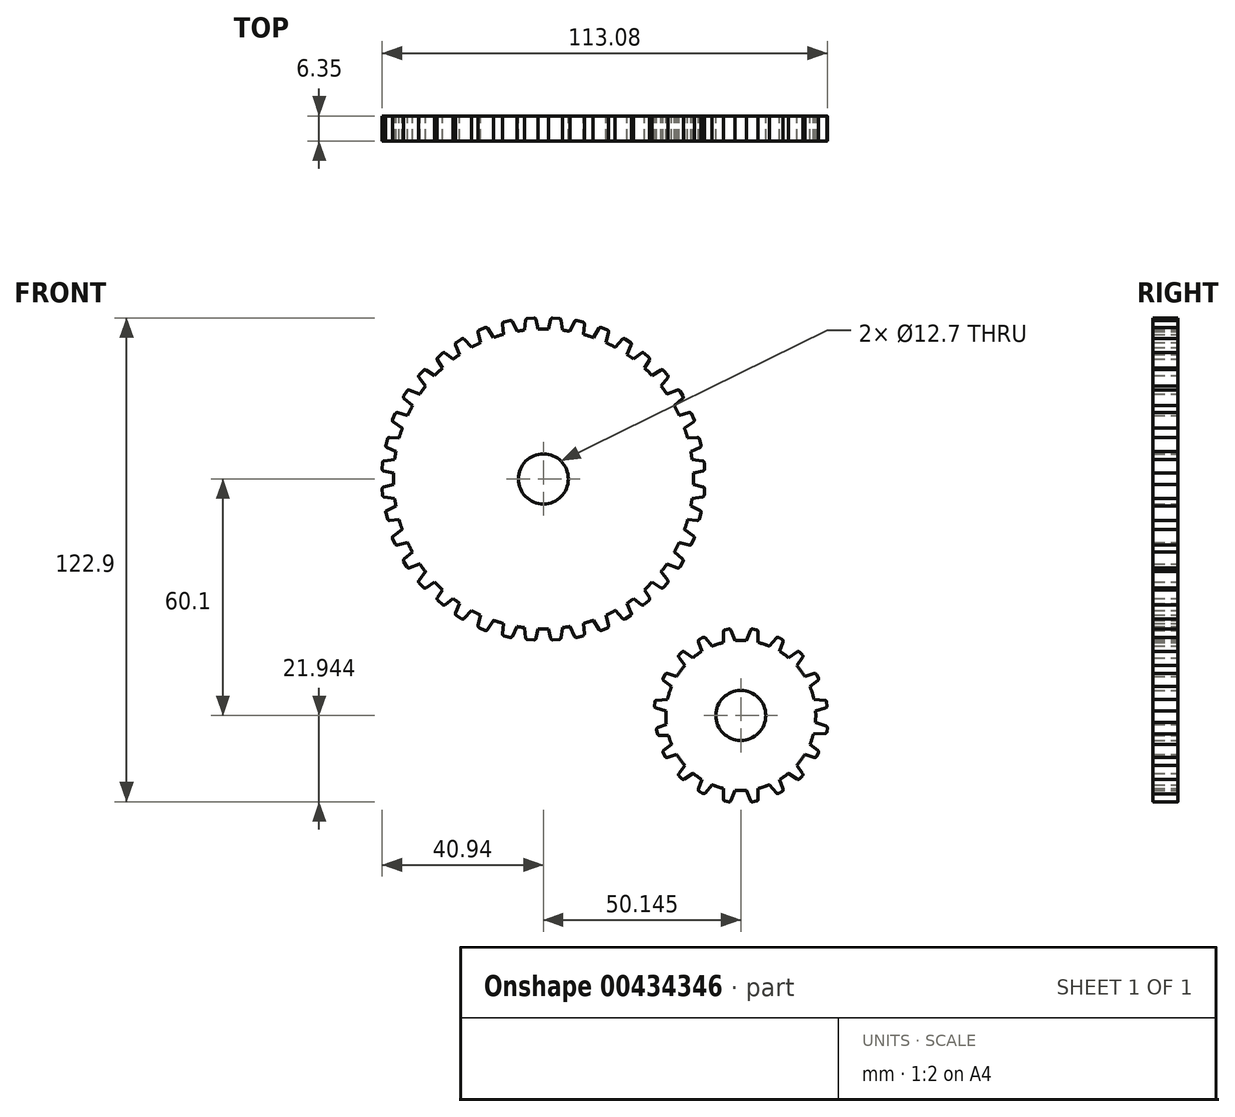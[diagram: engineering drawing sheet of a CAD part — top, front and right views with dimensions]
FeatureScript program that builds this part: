
annotation { "Feature Type Name" : "Feature", "Feature Type Description" : "" }
export const myFeature = defineFeature(function(context is Context, id is Id, definition is map)
    precondition{}
    {
        {
            var Q0;
            Q0=qCreatedBy(makeId("Front.planeOp"),FACE);
            var sketch = newSketch(context, id + "F0", { "sketchPlane" : qUnion([Q0])});
            skCircle(sketch, "E0", {"center": v(-27.1, 27.65) * mm, "radius": 38.1 * mm});
            skCircle(sketch, "E1", {"center": v(-27.1, 27.65) * mm, "radius": 6.35 * mm});
            skLineSegment(sketch, "E2", {"start": v(10.04, 32.06) * mm, "end": v(10.15, 29.52) * mm});
            skLineSegment(sketch, "E3", {"start": v(13.33, 32.24) * mm, "end": v(10.6, 32.59) * mm});
            skLineSegment(sketch, "E4", {"start": v(10.77, 29.05) * mm, "end": v(13.45, 29.65) * mm});
            skLineSegment(sketch, "E5", {"start": v(13.77, 31.76) * mm, "end": v(13.84, 30.17) * mm});
            skPoint(sketch, "E6.visualSharp", {"position": v(13.75, 32.18) * mm});
            skArc(sketch, "E6.filletArc", {"start": v(13.77, 31.76) * mm, "mid": v(13.64, 32.08) * mm, "end": v(13.33, 32.24) * mm});
            skPoint(sketch, "E7.visualSharp", {"position": v(10, 32.67) * mm});
            skArc(sketch, "E7.filletArc", {"start": v(10.6, 32.59) * mm, "mid": v(10.2, 32.46) * mm, "end": v(10.04, 32.06) * mm});
            skArc(sketch, "E8.filletArc", {"start": v(10.15, 29.52) * mm, "mid": v(10.35, 29.14) * mm, "end": v(10.77, 29.05) * mm});
            skPoint(sketch, "E9.visualSharp", {"position": v(13.86, 29.75) * mm});
            skArc(sketch, "E9.filletArc", {"start": v(13.45, 29.65) * mm, "mid": v(13.74, 29.84) * mm, "end": v(13.84, 30.17) * mm});
            skLineSegment(sketch, "E10.0", {"start": v(13.86, 29.75) * mm, "end": v(13.75, 32.18) * mm, "construction": true});
            skLineSegment(sketch, "E11", {"start": v(6.96, 43.07) * mm, "end": v(8.03, 40.77) * mm});
            skLineSegment(sketch, "E12", {"start": v(9.93, 44.48) * mm, "end": v(7.28, 43.77) * mm});
            skLineSegment(sketch, "E13", {"start": v(8.78, 40.57) * mm, "end": v(11.03, 42.14) * mm});
            skLineSegment(sketch, "E14", {"start": v(10.52, 44.2) * mm, "end": v(11.2, 42.77) * mm});
            skPoint(sketch, "E15.visualSharp", {"position": v(10.34, 44.6) * mm});
            skArc(sketch, "E15.filletArc", {"start": v(10.52, 44.2) * mm, "mid": v(10.28, 44.45) * mm, "end": v(9.93, 44.48) * mm});
            skPoint(sketch, "E16.visualSharp", {"position": v(6.7, 43.62) * mm});
            skArc(sketch, "E16.filletArc", {"start": v(7.28, 43.77) * mm, "mid": v(6.96, 43.5) * mm, "end": v(6.96, 43.07) * mm});
            skPoint(sketch, "E17.visualSharp", {"position": v(8.29, 40.22) * mm});
            skArc(sketch, "E17.filletArc", {"start": v(8.03, 40.77) * mm, "mid": v(8.36, 40.5) * mm, "end": v(8.78, 40.57) * mm});
            skPoint(sketch, "E18.visualSharp", {"position": v(11.38, 42.38) * mm});
            skArc(sketch, "E18.filletArc", {"start": v(11.03, 42.14) * mm, "mid": v(11.23, 42.42) * mm, "end": v(11.2, 42.77) * mm});
            skLineSegment(sketch, "E19.0", {"start": v(11.38, 42.38) * mm, "end": v(10.34, 44.6) * mm, "construction": true});
            skLineSegment(sketch, "E20", {"start": v(4.05, 48.5) * mm, "end": v(5.33, 46.32) * mm});
            skLineSegment(sketch, "E21", {"start": v(6.97, 50.23) * mm, "end": v(4.3, 49.24) * mm});
            skLineSegment(sketch, "E22", {"start": v(6.1, 46.19) * mm, "end": v(8.26, 48.02) * mm});
            skLineSegment(sketch, "E23", {"start": v(7.58, 50) * mm, "end": v(8.37, 48.67) * mm});
            skPoint(sketch, "E24.visualSharp", {"position": v(7.37, 50.38) * mm});
            skArc(sketch, "E24.filletArc", {"start": v(7.58, 50) * mm, "mid": v(7.32, 50.23) * mm, "end": v(6.97, 50.23) * mm});
            skPoint(sketch, "E25.visualSharp", {"position": v(3.74, 49.03) * mm});
            skArc(sketch, "E25.filletArc", {"start": v(4.3, 49.24) * mm, "mid": v(4, 48.94) * mm, "end": v(4.05, 48.5) * mm});
            skPoint(sketch, "E26.visualSharp", {"position": v(5.63, 45.8) * mm});
            skArc(sketch, "E26.filletArc", {"start": v(5.33, 46.32) * mm, "mid": v(5.68, 46.07) * mm, "end": v(6.1, 46.19) * mm});
            skPoint(sketch, "E27.visualSharp", {"position": v(8.58, 48.3) * mm});
            skArc(sketch, "E27.filletArc", {"start": v(8.26, 48.02) * mm, "mid": v(8.43, 48.32) * mm, "end": v(8.37, 48.67) * mm});
            skLineSegment(sketch, "E28.0", {"start": v(8.58, 48.3) * mm, "end": v(7.37, 50.38) * mm, "construction": true});
            skLineSegment(sketch, "E29", {"start": v(0.34, 53.06) * mm, "end": v(2.06, 51.19) * mm});
            skLineSegment(sketch, "E30", {"start": v(2.75, 55.3) * mm, "end": v(0.44, 53.83) * mm});
            skLineSegment(sketch, "E31", {"start": v(2.84, 51.22) * mm, "end": v(4.5, 53.4) * mm});
            skLineSegment(sketch, "E32", {"start": v(3.4, 55.22) * mm, "end": v(4.47, 54.06) * mm});
            skPoint(sketch, "E33.visualSharp", {"position": v(3.1, 55.54) * mm});
            skArc(sketch, "E33.filletArc", {"start": v(3.4, 55.22) * mm, "mid": v(3.09, 55.38) * mm, "end": v(2.75, 55.3) * mm});
            skPoint(sketch, "E34.visualSharp", {"position": v(-0.07, 53.5) * mm});
            skArc(sketch, "E34.filletArc", {"start": v(0.44, 53.83) * mm, "mid": v(0.2, 53.47) * mm, "end": v(0.34, 53.06) * mm});
            skPoint(sketch, "E35.visualSharp", {"position": v(2.47, 50.74) * mm});
            skArc(sketch, "E35.filletArc", {"start": v(2.06, 51.19) * mm, "mid": v(2.46, 51.03) * mm, "end": v(2.84, 51.22) * mm});
            skPoint(sketch, "E36.visualSharp", {"position": v(4.76, 53.74) * mm});
            skArc(sketch, "E36.filletArc", {"start": v(4.5, 53.4) * mm, "mid": v(4.6, 53.74) * mm, "end": v(4.47, 54.06) * mm});
            skLineSegment(sketch, "E37.0", {"start": v(4.76, 53.74) * mm, "end": v(3.1, 55.54) * mm, "construction": true});
            skLineSegment(sketch, "E38", {"start": v(-8.73, 60.35) * mm, "end": v(-6.6, 58.97) * mm});
            skLineSegment(sketch, "E39", {"start": v(-6.96, 63.13) * mm, "end": v(-8.82, 61.12) * mm});
            skLineSegment(sketch, "E40", {"start": v(-5.85, 59.2) * mm, "end": v(-4.79, 61.73) * mm});
            skLineSegment(sketch, "E41", {"start": v(-6.31, 63.21) * mm, "end": v(-4.98, 62.35) * mm});
            skPoint(sketch, "E42.visualSharp", {"position": v(-6.67, 63.44) * mm});
            skArc(sketch, "E42.filletArc", {"start": v(-6.31, 63.21) * mm, "mid": v(-6.65, 63.29) * mm, "end": v(-6.96, 63.13) * mm});
            skPoint(sketch, "E43.visualSharp", {"position": v(-9.24, 60.68) * mm});
            skArc(sketch, "E43.filletArc", {"start": v(-8.82, 61.12) * mm, "mid": v(-8.96, 60.71) * mm, "end": v(-8.73, 60.35) * mm});
            skPoint(sketch, "E44.visualSharp", {"position": v(-6.09, 58.64) * mm});
            skArc(sketch, "E44.filletArc", {"start": v(-6.6, 58.97) * mm, "mid": v(-6.17, 58.91) * mm, "end": v(-5.85, 59.2) * mm});
            skPoint(sketch, "E45.visualSharp", {"position": v(-4.62, 62.12) * mm});
            skArc(sketch, "E45.filletArc", {"start": v(-4.79, 61.73) * mm, "mid": v(-4.77, 62.07) * mm, "end": v(-4.98, 62.35) * mm});
            skLineSegment(sketch, "E46.0", {"start": v(-4.62, 62.12) * mm, "end": v(-6.67, 63.44) * mm, "construction": true});
            skLineSegment(sketch, "E47", {"start": v(-14.2, 62.88) * mm, "end": v(-11.86, 61.89) * mm});
            skLineSegment(sketch, "E48", {"start": v(-12.92, 65.94) * mm, "end": v(-14.42, 63.62) * mm});
            skLineSegment(sketch, "E49", {"start": v(-11.16, 62.24) * mm, "end": v(-10.54, 64.93) * mm});
            skLineSegment(sketch, "E50", {"start": v(-12.3, 66.13) * mm, "end": v(-10.84, 65.51) * mm});
            skPoint(sketch, "E51.visualSharp", {"position": v(-12.69, 66.3) * mm});
            skArc(sketch, "E51.filletArc", {"start": v(-12.3, 66.13) * mm, "mid": v(-12.64, 66.15) * mm, "end": v(-12.92, 65.94) * mm});
            skPoint(sketch, "E52.visualSharp", {"position": v(-14.75, 63.12) * mm});
            skArc(sketch, "E52.filletArc", {"start": v(-14.42, 63.62) * mm, "mid": v(-14.48, 63.2) * mm, "end": v(-14.2, 62.88) * mm});
            skPoint(sketch, "E53.visualSharp", {"position": v(-11.3, 61.65) * mm});
            skArc(sketch, "E53.filletArc", {"start": v(-11.86, 61.89) * mm, "mid": v(-11.43, 61.9) * mm, "end": v(-11.16, 62.24) * mm});
            skPoint(sketch, "E54.visualSharp", {"position": v(-10.45, 65.34) * mm});
            skArc(sketch, "E54.filletArc", {"start": v(-10.54, 64.93) * mm, "mid": v(-10.59, 65.27) * mm, "end": v(-10.84, 65.51) * mm});
            skLineSegment(sketch, "E55.0", {"start": v(-10.45, 65.34) * mm, "end": v(-12.69, 66.3) * mm, "construction": true});
            skLineSegment(sketch, "E56", {"start": v(-20.02, 64.46) * mm, "end": v(-17.57, 63.8) * mm});
            skLineSegment(sketch, "E57", {"start": v(-19.2, 67.65) * mm, "end": v(-20.35, 65.17) * mm});
            skLineSegment(sketch, "E58", {"start": v(-16.93, 64.25) * mm, "end": v(-16.7, 66.98) * mm});
            skLineSegment(sketch, "E59", {"start": v(-18.6, 67.93) * mm, "end": v(-17.07, 67.52) * mm});
            skPoint(sketch, "E60.visualSharp", {"position": v(-19.02, 68.04) * mm});
            skArc(sketch, "E60.filletArc", {"start": v(-18.6, 67.93) * mm, "mid": v(-18.95, 67.9) * mm, "end": v(-19.2, 67.65) * mm});
            skPoint(sketch, "E61.visualSharp", {"position": v(-20.6, 64.62) * mm});
            skArc(sketch, "E61.filletArc", {"start": v(-20.35, 65.17) * mm, "mid": v(-20.35, 64.74) * mm, "end": v(-20.02, 64.46) * mm});
            skPoint(sketch, "E62.visualSharp", {"position": v(-16.98, 63.65) * mm});
            skArc(sketch, "E62.filletArc", {"start": v(-17.57, 63.8) * mm, "mid": v(-17.15, 63.88) * mm, "end": v(-16.93, 64.25) * mm});
            skPoint(sketch, "E63.visualSharp", {"position": v(-16.66, 67.4) * mm});
            skArc(sketch, "E63.filletArc", {"start": v(-16.7, 66.98) * mm, "mid": v(-16.79, 67.32) * mm, "end": v(-17.07, 67.52) * mm});
            skLineSegment(sketch, "E64.0", {"start": v(-16.66, 67.4) * mm, "end": v(-19.02, 68.04) * mm, "construction": true});
            skLineSegment(sketch, "E65", {"start": v(8.98, 37.34) * mm, "end": v(9.63, 34.89) * mm});
            skLineSegment(sketch, "E66", {"start": v(11.97, 38.2) * mm, "end": v(9.42, 37.98) * mm});
            skLineSegment(sketch, "E67", {"start": v(10.34, 34.56) * mm, "end": v(12.66, 35.63) * mm});
            skLineSegment(sketch, "E68", {"start": v(12.5, 37.82) * mm, "end": v(12.93, 36.22) * mm});
            skPoint(sketch, "E69.visualSharp", {"position": v(12.4, 38.23) * mm});
            skArc(sketch, "E69.filletArc", {"start": v(12.5, 37.82) * mm, "mid": v(12.3, 38.1) * mm, "end": v(11.97, 38.2) * mm});
            skPoint(sketch, "E70.visualSharp", {"position": v(8.82, 37.92) * mm});
            skArc(sketch, "E70.filletArc", {"start": v(9.42, 37.98) * mm, "mid": v(9.05, 37.76) * mm, "end": v(8.98, 37.34) * mm});
            skPoint(sketch, "E71.visualSharp", {"position": v(9.79, 34.3) * mm});
            skArc(sketch, "E71.filletArc", {"start": v(9.63, 34.89) * mm, "mid": v(9.9, 34.56) * mm, "end": v(10.34, 34.56) * mm});
            skPoint(sketch, "E72.visualSharp", {"position": v(13.04, 35.81) * mm});
            skArc(sketch, "E72.filletArc", {"start": v(12.66, 35.63) * mm, "mid": v(12.9, 35.88) * mm, "end": v(12.93, 36.22) * mm});
            skLineSegment(sketch, "E73.0", {"start": v(13.04, 35.81) * mm, "end": v(12.4, 38.23) * mm, "construction": true});
            skLineSegment(sketch, "E74", {"start": v(-25.32, 65) * mm, "end": v(-22.78, 64.91) * mm});
            skLineSegment(sketch, "E75", {"start": v(-25.27, 68.11) * mm, "end": v(-25.8, 65.6) * mm});
            skLineSegment(sketch, "E76", {"start": v(-22.26, 65.49) * mm, "end": v(-22.62, 68.02) * mm});
            skLineSegment(sketch, "E77", {"start": v(-24.76, 68.51) * mm, "end": v(-23.1, 68.46) * mm});
            skPoint(sketch, "E78.visualSharp", {"position": v(-25.18, 68.53) * mm});
            skArc(sketch, "E78.filletArc", {"start": v(-24.76, 68.51) * mm, "mid": v(-25.09, 68.4) * mm, "end": v(-25.27, 68.11) * mm});
            skPoint(sketch, "E79.visualSharp", {"position": v(-25.93, 65.02) * mm});
            skArc(sketch, "E79.filletArc", {"start": v(-25.8, 65.6) * mm, "mid": v(-25.7, 65.2) * mm, "end": v(-25.32, 65) * mm});
            skPoint(sketch, "E80.visualSharp", {"position": v(-22.18, 64.9) * mm});
            skArc(sketch, "E80.filletArc", {"start": v(-22.78, 64.91) * mm, "mid": v(-22.39, 65.08) * mm, "end": v(-22.26, 65.49) * mm});
            skPoint(sketch, "E81.visualSharp", {"position": v(-22.68, 68.44) * mm});
            skArc(sketch, "E81.filletArc", {"start": v(-22.62, 68.02) * mm, "mid": v(-22.79, 68.33) * mm, "end": v(-23.1, 68.46) * mm});
            skLineSegment(sketch, "E82.0", {"start": v(-22.68, 68.44) * mm, "end": v(-25.18, 68.53) * mm, "construction": true});
            skPoint(sketch, "E83.endSnap0", {"position": v(10.7, 38.09) * mm});
            skLineSegment(sketch, "E84", {"start": v(-27.1, 65.75) * mm, "end": v(-27.1, -10.45) * mm, "construction": true});
            skLineSegment(sketch, "E85", {"start": v(-65.2, 27.65) * mm, "end": v(11, 27.65) * mm, "construction": true});
            skLineSegment(sketch, "E86", {"start": v(-4.21, 57.29) * mm, "end": v(-2.34, 55.57) * mm});
            skLineSegment(sketch, "E87", {"start": v(-2.15, 59.62) * mm, "end": v(-4.18, 58.06) * mm});
            skLineSegment(sketch, "E88", {"start": v(-1.57, 55.68) * mm, "end": v(-0.2, 57.84) * mm});
            skLineSegment(sketch, "E89", {"start": v(-1.5, 59.6) * mm, "end": v(-0.28, 58.48) * mm});
            skPoint(sketch, "E90.visualSharp", {"position": v(-1.82, 59.88) * mm});
            skArc(sketch, "E90.filletArc", {"start": v(-1.5, 59.6) * mm, "mid": v(-1.82, 59.73) * mm, "end": v(-2.15, 59.62) * mm});
            skPoint(sketch, "E91.visualSharp", {"position": v(-4.66, 57.7) * mm});
            skArc(sketch, "E91.filletArc", {"start": v(-4.18, 58.06) * mm, "mid": v(-4.38, 57.68) * mm, "end": v(-4.21, 57.29) * mm});
            skPoint(sketch, "E92.visualSharp", {"position": v(-1.9, 55.16) * mm});
            skArc(sketch, "E92.filletArc", {"start": v(-2.34, 55.57) * mm, "mid": v(-1.93, 55.44) * mm, "end": v(-1.57, 55.68) * mm});
            skPoint(sketch, "E93.visualSharp", {"position": v(0.03, 58.2) * mm});
            skArc(sketch, "E93.filletArc", {"start": v(-0.2, 57.84) * mm, "mid": v(-0.12, 58.17) * mm, "end": v(-0.28, 58.48) * mm});
            skLineSegment(sketch, "E94.0", {"start": v(0.03, 58.2) * mm, "end": v(-1.82, 59.88) * mm, "construction": true});
            skLineSegment(sketch, "E95.MirrorCS", {"start": v(-57.6, 55.22) * mm, "end": v(-58.67, 54.06) * mm});
            skArc(sketch, "E96.MirrorCS", {"start": v(-29.44, 68.51) * mm, "mid": v(-29.11, 68.4) * mm, "end": v(-28.93, 68.11) * mm});
            skArc(sketch, "E97.MirrorCS", {"start": v(-37.5, 66.98) * mm, "mid": v(-37.41, 67.32) * mm, "end": v(-37.13, 67.52) * mm});
            skLineSegment(sketch, "E98.MirrorCS", {"start": v(-61.78, 50) * mm, "end": v(-62.57, 48.67) * mm});
            skArc(sketch, "E99.MirrorCS", {"start": v(-66.7, 37.82) * mm, "mid": v(-66.5, 38.1) * mm, "end": v(-66.17, 38.2) * mm});
            skArc(sketch, "E100.MirrorCS", {"start": v(-43.66, 64.93) * mm, "mid": v(-43.61, 65.27) * mm, "end": v(-43.36, 65.51) * mm});
            skArc(sketch, "E101.MirrorCS", {"start": v(-63.62, 37.98) * mm, "mid": v(-63.25, 37.76) * mm, "end": v(-63.18, 37.34) * mm});
            skArc(sketch, "E102.MirrorCS", {"start": v(-33.85, 65.17) * mm, "mid": v(-33.85, 64.74) * mm, "end": v(-34.18, 64.46) * mm});
            skArc(sketch, "E103.MirrorCS", {"start": v(-49.42, 61.73) * mm, "mid": v(-49.43, 62.07) * mm, "end": v(-49.22, 62.35) * mm});
            skArc(sketch, "E104.MirrorCS", {"start": v(-64.8, 32.59) * mm, "mid": v(-64.4, 32.46) * mm, "end": v(-64.24, 32.06) * mm});
            skArc(sketch, "E105.MirrorCS", {"start": v(-50.02, 58.06) * mm, "mid": v(-49.82, 57.68) * mm, "end": v(-49.99, 57.29) * mm});
            skArc(sketch, "E106.MirrorCS", {"start": v(-66.86, 35.63) * mm, "mid": v(-67.1, 35.88) * mm, "end": v(-67.13, 36.22) * mm});
            skArc(sketch, "E107.MirrorCS", {"start": v(-54.64, 53.83) * mm, "mid": v(-54.4, 53.47) * mm, "end": v(-54.54, 53.06) * mm});
            skLineSegment(sketch, "E108.MirrorCS", {"start": v(-49.58, 62.12) * mm, "end": v(-47.53, 63.44) * mm, "construction": true});
            skArc(sketch, "E109.MirrorCS", {"start": v(-31.58, 68.02) * mm, "mid": v(-31.41, 68.33) * mm, "end": v(-31.1, 68.46) * mm});
            skArc(sketch, "E110.MirrorCS", {"start": v(-36.63, 63.8) * mm, "mid": v(-37.05, 63.88) * mm, "end": v(-37.27, 64.25) * mm});
            skArc(sketch, "E111.MirrorCS", {"start": v(-62.23, 40.77) * mm, "mid": v(-62.56, 40.5) * mm, "end": v(-62.98, 40.57) * mm});
            skLineSegment(sketch, "E112.MirrorCS", {"start": v(-43.75, 65.34) * mm, "end": v(-41.51, 66.3) * mm, "construction": true});
            skArc(sketch, "E113.MirrorCS", {"start": v(-39.78, 63.62) * mm, "mid": v(-39.72, 63.2) * mm, "end": v(-40, 62.88) * mm});
            skArc(sketch, "E114.MirrorCS", {"start": v(-31.42, 64.91) * mm, "mid": v(-31.81, 65.08) * mm, "end": v(-31.94, 65.49) * mm});
            skArc(sketch, "E115.MirrorCS", {"start": v(-62.46, 48.02) * mm, "mid": v(-62.63, 48.32) * mm, "end": v(-62.57, 48.67) * mm});
            skArc(sketch, "E116.MirrorCS", {"start": v(-64.35, 29.52) * mm, "mid": v(-64.55, 29.14) * mm, "end": v(-64.97, 29.05) * mm});
            skLineSegment(sketch, "E117.MirrorCS", {"start": v(-41.9, 66.13) * mm, "end": v(-43.36, 65.51) * mm});
            skArc(sketch, "E118.MirrorCS", {"start": v(-58.5, 49.24) * mm, "mid": v(-58.2, 48.94) * mm, "end": v(-58.25, 48.5) * mm});
            skArc(sketch, "E119.MirrorCS", {"start": v(-47.6, 58.97) * mm, "mid": v(-48.03, 58.91) * mm, "end": v(-48.35, 59.2) * mm});
            skArc(sketch, "E120.MirrorCS", {"start": v(-35.6, 67.93) * mm, "mid": v(-35.25, 67.9) * mm, "end": v(-35, 67.65) * mm});
            skLineSegment(sketch, "E121.MirrorCS", {"start": v(-47.89, 63.21) * mm, "end": v(-49.22, 62.35) * mm});
            skArc(sketch, "E122.MirrorCS", {"start": v(-67.97, 31.76) * mm, "mid": v(-67.84, 32.08) * mm, "end": v(-67.53, 32.24) * mm});
            skArc(sketch, "E123.MirrorCS", {"start": v(-59.53, 46.32) * mm, "mid": v(-59.88, 46.07) * mm, "end": v(-60.3, 46.19) * mm});
            skArc(sketch, "E124.MirrorCS", {"start": v(-47.89, 63.21) * mm, "mid": v(-47.55, 63.29) * mm, "end": v(-47.24, 63.13) * mm});
            skLineSegment(sketch, "E125.MirrorCS", {"start": v(-58.96, 53.74) * mm, "end": v(-57.3, 55.54) * mm, "construction": true});
            skArc(sketch, "E126.MirrorCS", {"start": v(-63.83, 34.89) * mm, "mid": v(-64.1, 34.56) * mm, "end": v(-64.54, 34.56) * mm});
            skLineSegment(sketch, "E127.MirrorCS", {"start": v(-62.78, 48.3) * mm, "end": v(-61.57, 50.38) * mm, "construction": true});
            skArc(sketch, "E128.MirrorCS", {"start": v(-51.86, 55.57) * mm, "mid": v(-52.27, 55.44) * mm, "end": v(-52.63, 55.68) * mm});
            skArc(sketch, "E129.MirrorCS", {"start": v(-64.73, 44.2) * mm, "mid": v(-64.48, 44.45) * mm, "end": v(-64.13, 44.48) * mm});
            skArc(sketch, "E130.MirrorCS", {"start": v(-54, 57.84) * mm, "mid": v(-54.08, 58.17) * mm, "end": v(-53.92, 58.48) * mm});
            skArc(sketch, "E131.MirrorCS", {"start": v(-61.78, 50) * mm, "mid": v(-61.52, 50.23) * mm, "end": v(-61.17, 50.23) * mm});
            skArc(sketch, "E132.MirrorCS", {"start": v(-45.38, 61.12) * mm, "mid": v(-45.24, 60.71) * mm, "end": v(-45.47, 60.35) * mm});
            skArc(sketch, "E133.MirrorCS", {"start": v(-58.7, 53.4) * mm, "mid": v(-58.8, 53.74) * mm, "end": v(-58.67, 54.06) * mm});
            skArc(sketch, "E134.MirrorCS", {"start": v(-52.7, 59.6) * mm, "mid": v(-52.38, 59.73) * mm, "end": v(-52.05, 59.62) * mm});
            skArc(sketch, "E135.MirrorCS", {"start": v(-56.26, 51.19) * mm, "mid": v(-56.66, 51.03) * mm, "end": v(-57.04, 51.22) * mm});
            skArc(sketch, "E136.MirrorCS", {"start": v(-42.34, 61.89) * mm, "mid": v(-42.77, 61.9) * mm, "end": v(-43.04, 62.24) * mm});
            skArc(sketch, "E137.MirrorCS", {"start": v(-65.23, 42.14) * mm, "mid": v(-65.43, 42.42) * mm, "end": v(-65.4, 42.77) * mm});
            skArc(sketch, "E138.MirrorCS", {"start": v(-57.6, 55.22) * mm, "mid": v(-57.29, 55.38) * mm, "end": v(-56.95, 55.3) * mm});
            skArc(sketch, "E139.MirrorCS", {"start": v(-61.49, 43.77) * mm, "mid": v(-61.16, 43.5) * mm, "end": v(-61.16, 43.07) * mm});
            skArc(sketch, "E140.MirrorCS", {"start": v(-28.4, 65.6) * mm, "mid": v(-28.5, 65.2) * mm, "end": v(-28.88, 65) * mm});
            skArc(sketch, "E141.MirrorCS", {"start": v(-41.9, 66.13) * mm, "mid": v(-41.56, 66.15) * mm, "end": v(-41.28, 65.94) * mm});
            skLineSegment(sketch, "E142.MirrorCS", {"start": v(-29.44, 68.51) * mm, "end": v(-31.1, 68.46) * mm});
            skLineSegment(sketch, "E143.MirrorCS", {"start": v(-52.7, 59.6) * mm, "end": v(-53.92, 58.48) * mm});
            skLineSegment(sketch, "E144.MirrorCS", {"start": v(-64.73, 44.2) * mm, "end": v(-65.4, 42.77) * mm});
            skLineSegment(sketch, "E145.MirrorCS", {"start": v(-66.7, 37.82) * mm, "end": v(-67.13, 36.22) * mm});
            skLineSegment(sketch, "E146.MirrorCS", {"start": v(-35.6, 67.93) * mm, "end": v(-37.13, 67.52) * mm});
            skLineSegment(sketch, "E147.MirrorCS", {"start": v(-66.17, 38.2) * mm, "end": v(-63.62, 37.98) * mm});
            skArc(sketch, "E148.MirrorCS", {"start": v(-67.65, 29.65) * mm, "mid": v(-67.94, 29.84) * mm, "end": v(-68.04, 30.17) * mm});
            skLineSegment(sketch, "E149.MirrorCS", {"start": v(-54.23, 58.2) * mm, "end": v(-52.38, 59.88) * mm, "construction": true});
            skLineSegment(sketch, "E150.MirrorCS", {"start": v(-28.88, 65) * mm, "end": v(-31.42, 64.91) * mm});
            skLineSegment(sketch, "E151.MirrorCS", {"start": v(-37.54, 67.4) * mm, "end": v(-35.18, 68.04) * mm, "construction": true});
            skLineSegment(sketch, "E152.MirrorCS", {"start": v(-31.52, 68.44) * mm, "end": v(-29.02, 68.53) * mm, "construction": true});
            skLineSegment(sketch, "E153.MirrorCS", {"start": v(-61.16, 43.07) * mm, "end": v(-62.23, 40.77) * mm});
            skLineSegment(sketch, "E154.MirrorCS", {"start": v(-67.97, 31.76) * mm, "end": v(-68.04, 30.17) * mm});
            skLineSegment(sketch, "E155.MirrorCS", {"start": v(-67.24, 35.81) * mm, "end": v(-66.6, 38.23) * mm, "construction": true});
            skLineSegment(sketch, "E156.MirrorCS", {"start": v(-40, 62.88) * mm, "end": v(-42.34, 61.89) * mm});
            skLineSegment(sketch, "E157.MirrorCS", {"start": v(-65.58, 42.38) * mm, "end": v(-64.55, 44.6) * mm, "construction": true});
            skLineSegment(sketch, "E158.MirrorCS", {"start": v(-34.18, 64.46) * mm, "end": v(-36.63, 63.8) * mm});
            skLineSegment(sketch, "E159.MirrorCS", {"start": v(-52.05, 59.62) * mm, "end": v(-50.02, 58.06) * mm});
            skPoint(sketch, "E160.MirrorP", {"position": v(-52.38, 59.88) * mm});
            skPoint(sketch, "E161.MirrorP", {"position": v(-47.53, 63.44) * mm});
            skLineSegment(sketch, "E162.MirrorCS", {"start": v(-52.63, 55.68) * mm, "end": v(-54, 57.84) * mm});
            skLineSegment(sketch, "E163.MirrorCS", {"start": v(-60.3, 46.19) * mm, "end": v(-62.46, 48.02) * mm});
            skPoint(sketch, "E164.MirrorP", {"position": v(-67.24, 35.81) * mm});
            skLineSegment(sketch, "E165.MirrorCS", {"start": v(-41.28, 65.94) * mm, "end": v(-39.78, 63.62) * mm});
            skPoint(sketch, "E166.MirrorP", {"position": v(-49.58, 62.12) * mm});
            skPoint(sketch, "E167.MirrorP", {"position": v(-62.78, 48.3) * mm});
            skLineSegment(sketch, "E168.MirrorCS", {"start": v(-54.54, 53.06) * mm, "end": v(-56.26, 51.19) * mm});
            skPoint(sketch, "E169.MirrorP", {"position": v(-31.52, 68.44) * mm});
            skPoint(sketch, "E170.MirrorP", {"position": v(-37.54, 67.4) * mm});
            skLineSegment(sketch, "E171.MirrorCS", {"start": v(-43.04, 62.24) * mm, "end": v(-43.66, 64.93) * mm});
            skLineSegment(sketch, "E172.MirrorCS", {"start": v(-37.27, 64.25) * mm, "end": v(-37.5, 66.98) * mm});
            skPoint(sketch, "E173.MirrorP", {"position": v(-37.22, 63.65) * mm});
            skLineSegment(sketch, "E174.MirrorCS", {"start": v(-56.95, 55.3) * mm, "end": v(-54.64, 53.83) * mm});
            skPoint(sketch, "E175.MirrorP", {"position": v(-64.55, 44.6) * mm});
            skPoint(sketch, "E176.MirrorP", {"position": v(-58.96, 53.74) * mm});
            skLineSegment(sketch, "E177.MirrorCS", {"start": v(-64.97, 29.05) * mm, "end": v(-67.65, 29.65) * mm});
            skLineSegment(sketch, "E178.MirrorCS", {"start": v(-31.94, 65.49) * mm, "end": v(-31.58, 68.02) * mm});
            skPoint(sketch, "E179.MirrorP", {"position": v(-63.02, 37.92) * mm});
            skPoint(sketch, "E180.MirrorP", {"position": v(-57.94, 49.03) * mm});
            skLineSegment(sketch, "E181.MirrorCS", {"start": v(-63.18, 37.34) * mm, "end": v(-63.83, 34.89) * mm});
            skLineSegment(sketch, "E182.MirrorCS", {"start": v(-62.98, 40.57) * mm, "end": v(-65.23, 42.14) * mm});
            skLineSegment(sketch, "E183.MirrorCS", {"start": v(-67.53, 32.24) * mm, "end": v(-64.8, 32.59) * mm});
            skLineSegment(sketch, "E184.MirrorCS", {"start": v(-57.04, 51.22) * mm, "end": v(-58.7, 53.4) * mm});
            skPoint(sketch, "E185.MirrorP", {"position": v(-52.3, 55.16) * mm});
            skPoint(sketch, "E186.MirrorP", {"position": v(-32.02, 64.9) * mm});
            skLineSegment(sketch, "E187.MirrorCS", {"start": v(-64.54, 34.56) * mm, "end": v(-66.86, 35.63) * mm});
            skPoint(sketch, "E188.MirrorP", {"position": v(-59.83, 45.8) * mm});
            skLineSegment(sketch, "E189.MirrorCS", {"start": v(-64.24, 32.06) * mm, "end": v(-64.35, 29.52) * mm});
            skPoint(sketch, "E190.MirrorP", {"position": v(-39.45, 63.12) * mm});
            skPoint(sketch, "E191.MirrorP", {"position": v(-61.57, 50.38) * mm});
            skPoint(sketch, "E192.MirrorP", {"position": v(-48.12, 58.64) * mm});
            skPoint(sketch, "E193.MirrorP", {"position": v(-64.9, 38.09) * mm});
            skPoint(sketch, "E194.MirrorP", {"position": v(-49.54, 57.7) * mm});
            skPoint(sketch, "E195.MirrorP", {"position": v(-66.6, 38.23) * mm});
            skPoint(sketch, "E196.MirrorP", {"position": v(-54.13, 53.5) * mm});
            skPoint(sketch, "E197.MirrorP", {"position": v(-54.23, 58.2) * mm});
            skPoint(sketch, "E198.MirrorP", {"position": v(-60.9, 43.62) * mm});
            skPoint(sketch, "E199.MirrorP", {"position": v(-64.2, 32.67) * mm});
            skLineSegment(sketch, "E200.MirrorCS", {"start": v(-28.93, 68.11) * mm, "end": v(-28.4, 65.6) * mm});
            skPoint(sketch, "E201.MirrorP", {"position": v(-33.6, 64.62) * mm});
            skLineSegment(sketch, "E202.MirrorCS", {"start": v(-45.47, 60.35) * mm, "end": v(-47.6, 58.97) * mm});
            skLineSegment(sketch, "E203.MirrorCS", {"start": v(-68.06, 29.75) * mm, "end": v(-67.95, 32.18) * mm, "construction": true});
            skPoint(sketch, "E204.MirrorP", {"position": v(-28.27, 65.02) * mm});
            skLineSegment(sketch, "E205.MirrorCS", {"start": v(-64.13, 44.48) * mm, "end": v(-61.49, 43.77) * mm});
            skLineSegment(sketch, "E206.MirrorCS", {"start": v(-35, 67.65) * mm, "end": v(-33.85, 65.17) * mm});
            skPoint(sketch, "E207.MirrorP", {"position": v(-44.96, 60.68) * mm});
            skLineSegment(sketch, "E208.MirrorCS", {"start": v(-47.24, 63.13) * mm, "end": v(-45.38, 61.12) * mm});
            skLineSegment(sketch, "E209.MirrorCS", {"start": v(-61.17, 50.23) * mm, "end": v(-58.5, 49.24) * mm});
            skLineSegment(sketch, "E210.MirrorCS", {"start": v(-49.99, 57.29) * mm, "end": v(-51.86, 55.57) * mm});
            skPoint(sketch, "E211.MirrorP", {"position": v(-63.99, 34.3) * mm});
            skPoint(sketch, "E212.MirrorP", {"position": v(-35.18, 68.04) * mm});
            skLineSegment(sketch, "E213.MirrorCS", {"start": v(-48.35, 59.2) * mm, "end": v(-49.42, 61.73) * mm});
            skPoint(sketch, "E214.MirrorP", {"position": v(-29.02, 68.53) * mm});
            skPoint(sketch, "E215.MirrorP", {"position": v(-65.58, 42.38) * mm});
            skPoint(sketch, "E216.MirrorP", {"position": v(-56.67, 50.74) * mm});
            skPoint(sketch, "E217.MirrorP", {"position": v(-42.9, 61.65) * mm});
            skPoint(sketch, "E218.MirrorP", {"position": v(-41.51, 66.3) * mm});
            skPoint(sketch, "E219.MirrorP", {"position": v(-57.3, 55.54) * mm});
            skPoint(sketch, "E220.MirrorP", {"position": v(-62.49, 40.22) * mm});
            skPoint(sketch, "E221.MirrorP", {"position": v(-43.75, 65.34) * mm});
            skLineSegment(sketch, "E222.MirrorCS", {"start": v(-58.25, 48.5) * mm, "end": v(-59.53, 46.32) * mm});
            skPoint(sketch, "E223.MirrorP", {"position": v(-68.06, 29.75) * mm});
            skPoint(sketch, "E224.MirrorP", {"position": v(-67.95, 32.18) * mm});
            skLineSegment(sketch, "E225.MirrorCS", {"start": v(11, 27.65) * mm, "end": v(-65.2, 27.65) * mm, "construction": true});
            skLineSegment(sketch, "E226.MirrorCS", {"start": v(3.4, 0.08) * mm, "end": v(4.47, 1.25) * mm});
            skLineSegment(sketch, "E227.MirrorCS", {"start": v(-18.6, -12.62) * mm, "end": v(-17.07, -12.21) * mm});
            skLineSegment(sketch, "E228.MirrorCS", {"start": v(7.58, 5.3) * mm, "end": v(8.37, 6.64) * mm});
            skLineSegment(sketch, "E229.MirrorCS", {"start": v(-52.7, -4.29) * mm, "end": v(-53.92, -3.18) * mm});
            skArc(sketch, "E230.MirrorCS", {"start": v(7.58, 5.3) * mm, "mid": v(7.32, 5.08) * mm, "end": v(6.97, 5.08) * mm});
            skArc(sketch, "E231.MirrorCS", {"start": v(-12.3, -10.82) * mm, "mid": v(-12.64, -10.84) * mm, "end": v(-12.92, -10.63) * mm});
            skLineSegment(sketch, "E232.MirrorCS", {"start": v(4.76, 1.56) * mm, "end": v(3.1, -0.23) * mm, "construction": true});
            skLineSegment(sketch, "E233.MirrorCS", {"start": v(-6.31, -7.9) * mm, "end": v(-4.98, -7.04) * mm});
            skLineSegment(sketch, "E234.MirrorCS", {"start": v(12.5, 17.49) * mm, "end": v(12.93, 19.08) * mm});
            skArc(sketch, "E235.MirrorCS", {"start": v(4.5, 1.9) * mm, "mid": v(4.6, 1.57) * mm, "end": v(4.47, 1.25) * mm});
            skArc(sketch, "E236.MirrorCS", {"start": v(3.4, 0.08) * mm, "mid": v(3.09, -0.08) * mm, "end": v(2.75, 0) * mm});
            skLineSegment(sketch, "E237.MirrorCS", {"start": v(-24.76, -13.2) * mm, "end": v(-23.1, -13.15) * mm});
            skArc(sketch, "E238.MirrorCS", {"start": v(-16.7, -11.68) * mm, "mid": v(-16.79, -12.01) * mm, "end": v(-17.07, -12.21) * mm});
            skLineSegment(sketch, "E239.MirrorCS", {"start": v(-61.78, 5.3) * mm, "end": v(-62.57, 6.64) * mm});
            skArc(sketch, "E240.MirrorCS", {"start": v(-18.6, -12.62) * mm, "mid": v(-18.95, -12.6) * mm, "end": v(-19.2, -12.35) * mm});
            skArc(sketch, "E241.MirrorCS", {"start": v(-24.76, -13.2) * mm, "mid": v(-25.09, -13.1) * mm, "end": v(-25.27, -12.8) * mm});
            skLineSegment(sketch, "E242.MirrorCS", {"start": v(-41.9, -10.82) * mm, "end": v(-43.36, -10.2) * mm});
            skLineSegment(sketch, "E243.MirrorCS", {"start": v(-1.5, -4.29) * mm, "end": v(-0.28, -3.18) * mm});
            skArc(sketch, "E244.MirrorCS", {"start": v(12.5, 17.49) * mm, "mid": v(12.3, 17.2) * mm, "end": v(11.97, 17.11) * mm});
            skLineSegment(sketch, "E245.MirrorCS", {"start": v(-12.3, -10.82) * mm, "end": v(-10.84, -10.2) * mm});
            skArc(sketch, "E246.MirrorCS", {"start": v(-4.79, -6.42) * mm, "mid": v(-4.77, -6.77) * mm, "end": v(-4.98, -7.04) * mm});
            skArc(sketch, "E247.MirrorCS", {"start": v(-1.5, -4.29) * mm, "mid": v(-1.82, -4.42) * mm, "end": v(-2.15, -4.32) * mm});
            skLineSegment(sketch, "E248.MirrorCS", {"start": v(-35.6, -12.62) * mm, "end": v(-37.13, -12.21) * mm});
            skLineSegment(sketch, "E249.MirrorCS", {"start": v(-66.7, 17.49) * mm, "end": v(-67.13, 19.08) * mm});
            skArc(sketch, "E250.MirrorCS", {"start": v(-56.26, 4.12) * mm, "mid": v(-56.66, 4.28) * mm, "end": v(-57.04, 4.08) * mm});
            skLineSegment(sketch, "E251.MirrorCS", {"start": v(-43.75, -10.04) * mm, "end": v(-41.51, -10.99) * mm, "construction": true});
            skLineSegment(sketch, "E252.MirrorCS", {"start": v(-29.44, -13.2) * mm, "end": v(-31.1, -13.15) * mm});
            skArc(sketch, "E253.MirrorCS", {"start": v(-45.38, -5.81) * mm, "mid": v(-45.24, -5.4) * mm, "end": v(-45.47, -5.04) * mm});
            skLineSegment(sketch, "E254.MirrorCS", {"start": v(-54.23, -2.89) * mm, "end": v(-52.38, -4.58) * mm, "construction": true});
            skArc(sketch, "E255.MirrorCS", {"start": v(-6.31, -7.9) * mm, "mid": v(-6.65, -7.98) * mm, "end": v(-6.96, -7.82) * mm});
            skArc(sketch, "E256.MirrorCS", {"start": v(-47.6, -3.66) * mm, "mid": v(-48.03, -3.6) * mm, "end": v(-48.35, -3.9) * mm});
            skArc(sketch, "E257.MirrorCS", {"start": v(-64.8, 22.72) * mm, "mid": v(-64.4, 22.85) * mm, "end": v(-64.24, 23.25) * mm});
            skArc(sketch, "E258.MirrorCS", {"start": v(5.33, 8.99) * mm, "mid": v(5.68, 9.23) * mm, "end": v(6.1, 9.12) * mm});
            skArc(sketch, "E259.MirrorCS", {"start": v(-65.23, 13.17) * mm, "mid": v(-65.43, 12.88) * mm, "end": v(-65.4, 12.54) * mm});
            skLineSegment(sketch, "E260.MirrorCS", {"start": v(-64.73, 11.1) * mm, "end": v(-65.4, 12.54) * mm});
            skArc(sketch, "E261.MirrorCS", {"start": v(-36.63, -8.5) * mm, "mid": v(-37.05, -8.57) * mm, "end": v(-37.27, -8.95) * mm});
            skArc(sketch, "E262.MirrorCS", {"start": v(-58.7, 1.9) * mm, "mid": v(-58.8, 1.57) * mm, "end": v(-58.67, 1.25) * mm});
            skArc(sketch, "E263.MirrorCS", {"start": v(-6.6, -3.66) * mm, "mid": v(-6.17, -3.6) * mm, "end": v(-5.85, -3.9) * mm});
            skArc(sketch, "E264.MirrorCS", {"start": v(-47.89, -7.9) * mm, "mid": v(-47.55, -7.98) * mm, "end": v(-47.24, -7.82) * mm});
            skLineSegment(sketch, "E265.MirrorCS", {"start": v(10.52, 11.1) * mm, "end": v(11.2, 12.54) * mm});
            skLineSegment(sketch, "E266.MirrorCS", {"start": v(-62.78, 7) * mm, "end": v(-61.57, 4.93) * mm, "construction": true});
            skArc(sketch, "E267.MirrorCS", {"start": v(-41.9, -10.82) * mm, "mid": v(-41.56, -10.84) * mm, "end": v(-41.28, -10.63) * mm});
            skLineSegment(sketch, "E268.MirrorCS", {"start": v(8.58, 7) * mm, "end": v(7.37, 4.93) * mm, "construction": true});
            skArc(sketch, "E269.MirrorCS", {"start": v(10.52, 11.1) * mm, "mid": v(10.28, 10.85) * mm, "end": v(9.93, 10.82) * mm});
            skArc(sketch, "E270.MirrorCS", {"start": v(-31.42, -9.6) * mm, "mid": v(-31.81, -9.77) * mm, "end": v(-31.94, -10.18) * mm});
            skArc(sketch, "E271.MirrorCS", {"start": v(-50.02, -2.76) * mm, "mid": v(-49.82, -2.38) * mm, "end": v(-49.99, -1.98) * mm});
            skArc(sketch, "E272.MirrorCS", {"start": v(12.66, 19.67) * mm, "mid": v(12.9, 19.43) * mm, "end": v(12.93, 19.08) * mm});
            skArc(sketch, "E273.MirrorCS", {"start": v(9.42, 17.33) * mm, "mid": v(9.05, 17.54) * mm, "end": v(8.98, 17.97) * mm});
            skArc(sketch, "E274.MirrorCS", {"start": v(-33.85, -9.86) * mm, "mid": v(-33.85, -9.43) * mm, "end": v(-34.18, -9.15) * mm});
            skArc(sketch, "E275.MirrorCS", {"start": v(-66.86, 19.67) * mm, "mid": v(-67.1, 19.43) * mm, "end": v(-67.13, 19.08) * mm});
            skArc(sketch, "E276.MirrorCS", {"start": v(0.44, 1.48) * mm, "mid": v(0.2, 1.84) * mm, "end": v(0.34, 2.25) * mm});
            skArc(sketch, "E277.MirrorCS", {"start": v(-28.4, -10.3) * mm, "mid": v(-28.5, -9.88) * mm, "end": v(-28.88, -9.69) * mm});
            skArc(sketch, "E278.MirrorCS", {"start": v(-59.53, 8.99) * mm, "mid": v(-59.88, 9.23) * mm, "end": v(-60.3, 9.12) * mm});
            skArc(sketch, "E279.MirrorCS", {"start": v(-61.78, 5.3) * mm, "mid": v(-61.52, 5.08) * mm, "end": v(-61.17, 5.08) * mm});
            skLineSegment(sketch, "E280.MirrorCS", {"start": v(-65.58, 12.92) * mm, "end": v(-64.55, 10.71) * mm, "construction": true});
            skLineSegment(sketch, "E281.MirrorCS", {"start": v(11.38, 12.92) * mm, "end": v(10.34, 10.71) * mm, "construction": true});
            skLineSegment(sketch, "E282.MirrorCS", {"start": v(-47.89, -7.9) * mm, "end": v(-49.22, -7.04) * mm});
            skArc(sketch, "E283.MirrorCS", {"start": v(-0.2, -2.53) * mm, "mid": v(-0.12, -2.87) * mm, "end": v(-0.28, -3.18) * mm});
            skArc(sketch, "E284.MirrorCS", {"start": v(-54.64, 1.48) * mm, "mid": v(-54.4, 1.84) * mm, "end": v(-54.54, 2.25) * mm});
            skLineSegment(sketch, "E285.MirrorCS", {"start": v(-31.52, -13.14) * mm, "end": v(-29.02, -13.22) * mm, "construction": true});
            skArc(sketch, "E286.MirrorCS", {"start": v(-49.42, -6.42) * mm, "mid": v(-49.43, -6.77) * mm, "end": v(-49.22, -7.04) * mm});
            skArc(sketch, "E287.MirrorCS", {"start": v(-31.58, -12.72) * mm, "mid": v(-31.41, -13.02) * mm, "end": v(-31.1, -13.15) * mm});
            skLineSegment(sketch, "E288.MirrorCS", {"start": v(-58.96, 1.56) * mm, "end": v(-57.3, -0.23) * mm, "construction": true});
            skArc(sketch, "E289.MirrorCS", {"start": v(-35.6, -12.62) * mm, "mid": v(-35.25, -12.6) * mm, "end": v(-35, -12.35) * mm});
            skLineSegment(sketch, "E290.MirrorCS", {"start": v(-37.54, -12.1) * mm, "end": v(-35.18, -12.73) * mm, "construction": true});
            skLineSegment(sketch, "E291.MirrorCS", {"start": v(-49.58, -6.81) * mm, "end": v(-47.53, -8.14) * mm, "construction": true});
            skArc(sketch, "E292.MirrorCS", {"start": v(-39.78, -8.32) * mm, "mid": v(-39.72, -7.9) * mm, "end": v(-40, -7.57) * mm});
            skArc(sketch, "E293.MirrorCS", {"start": v(9.63, 20.42) * mm, "mid": v(9.9, 20.75) * mm, "end": v(10.34, 20.75) * mm});
            skArc(sketch, "E294.MirrorCS", {"start": v(4.3, 6.06) * mm, "mid": v(4, 6.37) * mm, "end": v(4.05, 6.8) * mm});
            skArc(sketch, "E295.MirrorCS", {"start": v(-42.34, -6.58) * mm, "mid": v(-42.77, -6.6) * mm, "end": v(-43.04, -6.94) * mm});
            skArc(sketch, "E296.MirrorCS", {"start": v(-2.34, -0.27) * mm, "mid": v(-1.93, -0.14) * mm, "end": v(-1.57, -0.37) * mm});
            skArc(sketch, "E297.MirrorCS", {"start": v(-63.62, 17.33) * mm, "mid": v(-63.25, 17.54) * mm, "end": v(-63.18, 17.97) * mm});
            skLineSegment(sketch, "E298.MirrorCS", {"start": v(-10.45, -10.04) * mm, "end": v(-12.69, -10.99) * mm, "construction": true});
            skLineSegment(sketch, "E299.MirrorCS", {"start": v(-67.24, 19.5) * mm, "end": v(-66.6, 17.07) * mm, "construction": true});
            skArc(sketch, "E300.MirrorCS", {"start": v(13.77, 23.55) * mm, "mid": v(13.64, 23.23) * mm, "end": v(13.33, 23.07) * mm});
            skArc(sketch, "E301.MirrorCS", {"start": v(-64.73, 11.1) * mm, "mid": v(-64.48, 10.85) * mm, "end": v(-64.13, 10.82) * mm});
            skArc(sketch, "E302.MirrorCS", {"start": v(2.06, 4.12) * mm, "mid": v(2.46, 4.28) * mm, "end": v(2.84, 4.08) * mm});
            skArc(sketch, "E303.MirrorCS", {"start": v(-66.7, 17.49) * mm, "mid": v(-66.5, 17.2) * mm, "end": v(-66.17, 17.11) * mm});
            skArc(sketch, "E304.MirrorCS", {"start": v(-62.23, 14.54) * mm, "mid": v(-62.56, 14.82) * mm, "end": v(-62.98, 14.74) * mm});
            skArc(sketch, "E305.MirrorCS", {"start": v(-4.18, -2.76) * mm, "mid": v(-4.38, -2.38) * mm, "end": v(-4.21, -1.98) * mm});
            skLineSegment(sketch, "E306.MirrorCS", {"start": v(13.04, 19.5) * mm, "end": v(12.4, 17.07) * mm, "construction": true});
            skArc(sketch, "E307.MirrorCS", {"start": v(-17.57, -8.5) * mm, "mid": v(-17.15, -8.57) * mm, "end": v(-16.93, -8.95) * mm});
            skLineSegment(sketch, "E308.MirrorCS", {"start": v(-16.66, -12.1) * mm, "end": v(-19.02, -12.73) * mm, "construction": true});
            skArc(sketch, "E309.MirrorCS", {"start": v(7.28, 11.53) * mm, "mid": v(6.96, 11.8) * mm, "end": v(6.96, 12.24) * mm});
            skArc(sketch, "E310.MirrorCS", {"start": v(-63.83, 20.42) * mm, "mid": v(-64.1, 20.75) * mm, "end": v(-64.54, 20.75) * mm});
            skLineSegment(sketch, "E311.MirrorCS", {"start": v(-57.6, 0.08) * mm, "end": v(-58.67, 1.25) * mm});
            skArc(sketch, "E312.MirrorCS", {"start": v(-57.6, 0.08) * mm, "mid": v(-57.29, -0.08) * mm, "end": v(-56.95, 0) * mm});
            skArc(sketch, "E313.MirrorCS", {"start": v(-62.46, 7.29) * mm, "mid": v(-62.63, 6.98) * mm, "end": v(-62.57, 6.64) * mm});
            skArc(sketch, "E314.MirrorCS", {"start": v(-25.8, -10.3) * mm, "mid": v(-25.7, -9.88) * mm, "end": v(-25.32, -9.69) * mm});
            skArc(sketch, "E315.MirrorCS", {"start": v(10.15, 25.78) * mm, "mid": v(10.35, 26.16) * mm, "end": v(10.77, 26.25) * mm});
            skArc(sketch, "E316.MirrorCS", {"start": v(-14.42, -8.32) * mm, "mid": v(-14.48, -7.9) * mm, "end": v(-14.2, -7.57) * mm});
            skArc(sketch, "E317.MirrorCS", {"start": v(11.03, 13.17) * mm, "mid": v(11.23, 12.88) * mm, "end": v(11.2, 12.54) * mm});
            skArc(sketch, "E318.MirrorCS", {"start": v(-52.7, -4.29) * mm, "mid": v(-52.38, -4.42) * mm, "end": v(-52.05, -4.32) * mm});
            skArc(sketch, "E319.MirrorCS", {"start": v(-10.54, -9.62) * mm, "mid": v(-10.59, -9.97) * mm, "end": v(-10.84, -10.2) * mm});
            skArc(sketch, "E320.MirrorCS", {"start": v(8.03, 14.54) * mm, "mid": v(8.36, 14.82) * mm, "end": v(8.78, 14.74) * mm});
            skArc(sketch, "E321.MirrorCS", {"start": v(-11.86, -6.58) * mm, "mid": v(-11.43, -6.6) * mm, "end": v(-11.16, -6.94) * mm});
            skArc(sketch, "E322.MirrorCS", {"start": v(-51.86, -0.27) * mm, "mid": v(-52.27, -0.14) * mm, "end": v(-52.63, -0.37) * mm});
            skArc(sketch, "E323.MirrorCS", {"start": v(-58.5, 6.06) * mm, "mid": v(-58.2, 6.37) * mm, "end": v(-58.25, 6.8) * mm});
            skArc(sketch, "E324.MirrorCS", {"start": v(8.26, 7.29) * mm, "mid": v(8.43, 6.98) * mm, "end": v(8.37, 6.64) * mm});
            skArc(sketch, "E325.MirrorCS", {"start": v(-8.82, -5.81) * mm, "mid": v(-8.96, -5.4) * mm, "end": v(-8.73, -5.04) * mm});
            skArc(sketch, "E326.MirrorCS", {"start": v(-22.78, -9.6) * mm, "mid": v(-22.39, -9.77) * mm, "end": v(-22.26, -10.18) * mm});
            skArc(sketch, "E327.MirrorCS", {"start": v(-43.66, -9.62) * mm, "mid": v(-43.61, -9.97) * mm, "end": v(-43.36, -10.2) * mm});
            skArc(sketch, "E328.MirrorCS", {"start": v(-29.44, -13.2) * mm, "mid": v(-29.11, -13.1) * mm, "end": v(-28.93, -12.8) * mm});
            skLineSegment(sketch, "E329.MirrorCS", {"start": v(-22.68, -13.14) * mm, "end": v(-25.18, -13.22) * mm, "construction": true});
            skArc(sketch, "E330.MirrorCS", {"start": v(-64.35, 25.78) * mm, "mid": v(-64.55, 26.16) * mm, "end": v(-64.97, 26.25) * mm});
            skLineSegment(sketch, "E331.MirrorCS", {"start": v(0.03, -2.89) * mm, "end": v(-1.82, -4.58) * mm, "construction": true});
            skArc(sketch, "E332.MirrorCS", {"start": v(-54, -2.53) * mm, "mid": v(-54.08, -2.87) * mm, "end": v(-53.92, -3.18) * mm});
            skArc(sketch, "E333.MirrorCS", {"start": v(-22.62, -12.72) * mm, "mid": v(-22.79, -13.02) * mm, "end": v(-23.1, -13.15) * mm});
            skLineSegment(sketch, "E334.MirrorCS", {"start": v(-4.62, -6.81) * mm, "end": v(-6.67, -8.14) * mm, "construction": true});
            skArc(sketch, "E335.MirrorCS", {"start": v(-67.97, 23.55) * mm, "mid": v(-67.84, 23.23) * mm, "end": v(-67.53, 23.07) * mm});
            skArc(sketch, "E336.MirrorCS", {"start": v(10.6, 22.72) * mm, "mid": v(10.2, 22.85) * mm, "end": v(10.04, 23.25) * mm});
            skArc(sketch, "E337.MirrorCS", {"start": v(-37.5, -11.68) * mm, "mid": v(-37.41, -12.01) * mm, "end": v(-37.13, -12.21) * mm});
            skArc(sketch, "E338.MirrorCS", {"start": v(-61.49, 11.53) * mm, "mid": v(-61.16, 11.8) * mm, "end": v(-61.16, 12.24) * mm});
            skArc(sketch, "E339.MirrorCS", {"start": v(-20.35, -9.86) * mm, "mid": v(-20.35, -9.43) * mm, "end": v(-20.02, -9.15) * mm});
            skLineSegment(sketch, "E340.MirrorCS", {"start": v(-67.97, 23.55) * mm, "end": v(-68.04, 25.13) * mm});
            skLineSegment(sketch, "E341.MirrorCS", {"start": v(13.77, 23.55) * mm, "end": v(13.84, 25.13) * mm});
            skLineSegment(sketch, "E342.MirrorCS", {"start": v(13.86, 25.56) * mm, "end": v(13.75, 23.12) * mm, "construction": true});
            skLineSegment(sketch, "E343.MirrorCS", {"start": v(-68.06, 25.56) * mm, "end": v(-67.95, 23.12) * mm, "construction": true});
            skArc(sketch, "E344.MirrorCS", {"start": v(13.45, 25.65) * mm, "mid": v(13.74, 25.47) * mm, "end": v(13.84, 25.13) * mm});
            skLineSegment(sketch, "E345.MirrorCS", {"start": v(-66.17, 17.11) * mm, "end": v(-63.62, 17.33) * mm});
            skLineSegment(sketch, "E346.MirrorCS", {"start": v(11.97, 17.11) * mm, "end": v(9.42, 17.33) * mm});
            skArc(sketch, "E347.MirrorCS", {"start": v(-67.65, 25.65) * mm, "mid": v(-67.94, 25.47) * mm, "end": v(-68.04, 25.13) * mm});
            skLineSegment(sketch, "E348.MirrorCS", {"start": v(10.77, 26.25) * mm, "end": v(13.45, 25.65) * mm});
            skLineSegment(sketch, "E349.MirrorCS", {"start": v(10.04, 23.25) * mm, "end": v(10.15, 25.78) * mm});
            skLineSegment(sketch, "E350.MirrorCS", {"start": v(6.97, 5.08) * mm, "end": v(4.3, 6.06) * mm});
            skLineSegment(sketch, "E351.MirrorCS", {"start": v(-6.96, -7.82) * mm, "end": v(-8.82, -5.81) * mm});
            skLineSegment(sketch, "E352.MirrorCS", {"start": v(-16.93, -8.95) * mm, "end": v(-16.7, -11.68) * mm});
            skLineSegment(sketch, "E353.MirrorCS", {"start": v(0.34, 2.25) * mm, "end": v(2.06, 4.12) * mm});
            skLineSegment(sketch, "E354.MirrorCS", {"start": v(-20.02, -9.15) * mm, "end": v(-17.57, -8.5) * mm});
            skLineSegment(sketch, "E355.MirrorCS", {"start": v(10.34, 20.75) * mm, "end": v(12.66, 19.67) * mm});
            skLineSegment(sketch, "E356.MirrorCS", {"start": v(13.33, 23.07) * mm, "end": v(10.6, 22.72) * mm});
            skLineSegment(sketch, "E357.MirrorCS", {"start": v(-8.73, -5.04) * mm, "end": v(-6.6, -3.66) * mm});
            skLineSegment(sketch, "E358.MirrorCS", {"start": v(-14.2, -7.57) * mm, "end": v(-11.86, -6.58) * mm});
            skLineSegment(sketch, "E359.MirrorCS", {"start": v(-2.15, -4.32) * mm, "end": v(-4.18, -2.76) * mm});
            skLineSegment(sketch, "E360.MirrorCS", {"start": v(6.1, 9.12) * mm, "end": v(8.26, 7.29) * mm});
            skLineSegment(sketch, "E361.MirrorCS", {"start": v(-22.26, -10.18) * mm, "end": v(-22.62, -12.72) * mm});
            skLineSegment(sketch, "E362.MirrorCS", {"start": v(9.93, 10.82) * mm, "end": v(7.28, 11.53) * mm});
            skLineSegment(sketch, "E363.MirrorCS", {"start": v(2.84, 4.08) * mm, "end": v(4.5, 1.9) * mm});
            skLineSegment(sketch, "E364.MirrorCS", {"start": v(-1.57, -0.37) * mm, "end": v(-0.2, -2.53) * mm});
            skLineSegment(sketch, "E365.MirrorCS", {"start": v(4.05, 6.8) * mm, "end": v(5.33, 8.99) * mm});
            skLineSegment(sketch, "E366.MirrorCS", {"start": v(-12.92, -10.63) * mm, "end": v(-14.42, -8.32) * mm});
            skLineSegment(sketch, "E367.MirrorCS", {"start": v(8.98, 17.97) * mm, "end": v(9.63, 20.42) * mm});
            skLineSegment(sketch, "E368.MirrorCS", {"start": v(-11.16, -6.94) * mm, "end": v(-10.54, -9.62) * mm});
            skLineSegment(sketch, "E369.MirrorCS", {"start": v(-5.85, -3.9) * mm, "end": v(-4.79, -6.42) * mm});
            skLineSegment(sketch, "E370.MirrorCS", {"start": v(8.78, 14.74) * mm, "end": v(11.03, 13.17) * mm});
            skLineSegment(sketch, "E371.MirrorCS", {"start": v(-25.32, -9.69) * mm, "end": v(-22.78, -9.6) * mm});
            skLineSegment(sketch, "E372.MirrorCS", {"start": v(-4.21, -1.98) * mm, "end": v(-2.34, -0.27) * mm});
            skLineSegment(sketch, "E373.MirrorCS", {"start": v(2.75, 0) * mm, "end": v(0.44, 1.48) * mm});
            skLineSegment(sketch, "E374.MirrorCS", {"start": v(6.96, 12.24) * mm, "end": v(8.03, 14.54) * mm});
            skLineSegment(sketch, "E375.MirrorCS", {"start": v(-25.27, -12.8) * mm, "end": v(-25.8, -10.3) * mm});
            skLineSegment(sketch, "E376.MirrorCS", {"start": v(-52.05, -4.32) * mm, "end": v(-50.02, -2.76) * mm});
            skPoint(sketch, "E377.MirrorP", {"position": v(-25.93, -9.7) * mm});
            skPoint(sketch, "E378.MirrorP", {"position": v(-63.99, 21) * mm});
            skPoint(sketch, "E379.MirrorP", {"position": v(-52.3, 0.14) * mm});
            skLineSegment(sketch, "E380.MirrorCS", {"start": v(-45.47, -5.04) * mm, "end": v(-47.6, -3.66) * mm});
            skPoint(sketch, "E381.MirrorP", {"position": v(5.63, 9.51) * mm});
            skLineSegment(sketch, "E382.MirrorCS", {"start": v(-64.97, 26.25) * mm, "end": v(-67.65, 25.65) * mm});
            skLineSegment(sketch, "E383.MirrorCS", {"start": v(-54.54, 2.25) * mm, "end": v(-56.26, 4.12) * mm});
            skPoint(sketch, "E384.MirrorP", {"position": v(-22.18, -9.58) * mm});
            skPoint(sketch, "E385.MirrorP", {"position": v(-16.98, -8.34) * mm});
            skPoint(sketch, "E386.MirrorP", {"position": v(-6.09, -3.34) * mm});
            skLineSegment(sketch, "E387.MirrorCS", {"start": v(-61.17, 5.08) * mm, "end": v(-58.5, 6.06) * mm});
            skPoint(sketch, "E388.MirrorP", {"position": v(-28.27, -9.7) * mm});
            skPoint(sketch, "E389.MirrorP", {"position": v(-25.18, -13.22) * mm});
            skPoint(sketch, "E390.MirrorP", {"position": v(-63.02, 17.38) * mm});
            skPoint(sketch, "E391.MirrorP", {"position": v(3.1, -0.23) * mm});
            skPoint(sketch, "E392.MirrorP", {"position": v(-20.6, -9.31) * mm});
            skPoint(sketch, "E393.MirrorP", {"position": v(-9.24, -5.37) * mm});
            skLineSegment(sketch, "E394.MirrorCS", {"start": v(-57.04, 4.08) * mm, "end": v(-58.7, 1.9) * mm});
            skLineSegment(sketch, "E395.MirrorCS", {"start": v(-48.35, -3.9) * mm, "end": v(-49.42, -6.42) * mm});
            skLineSegment(sketch, "E396.MirrorCS", {"start": v(-63.18, 17.97) * mm, "end": v(-63.83, 20.42) * mm});
            skPoint(sketch, "E397.MirrorP", {"position": v(-56.67, 4.56) * mm});
            skPoint(sketch, "E398.MirrorP", {"position": v(-41.51, -10.99) * mm});
            skPoint(sketch, "E399.MirrorP", {"position": v(10, 22.64) * mm});
            skLineSegment(sketch, "E400.MirrorCS", {"start": v(-40, -7.57) * mm, "end": v(-42.34, -6.58) * mm});
            skLineSegment(sketch, "E401.MirrorCS", {"start": v(-62.98, 14.74) * mm, "end": v(-65.23, 13.17) * mm});
            skPoint(sketch, "E402.MirrorP", {"position": v(-60.9, 11.69) * mm});
            skPoint(sketch, "E403.MirrorP", {"position": v(2.47, 4.56) * mm});
            skPoint(sketch, "E404.MirrorP", {"position": v(-54.13, 1.8) * mm});
            skPoint(sketch, "E405.MirrorP", {"position": v(-43.75, -10.04) * mm});
            skPoint(sketch, "E406.MirrorP", {"position": v(-64.2, 22.64) * mm});
            skPoint(sketch, "E407.MirrorP", {"position": v(-4.66, -2.39) * mm});
            skLineSegment(sketch, "E408.MirrorCS", {"start": v(-64.24, 23.25) * mm, "end": v(-64.35, 25.78) * mm});
            skPoint(sketch, "E409.MirrorP", {"position": v(-57.94, 6.27) * mm});
            skPoint(sketch, "E410.MirrorP", {"position": v(-10.45, -10.04) * mm});
            skPoint(sketch, "E411.MirrorP", {"position": v(7.37, 4.93) * mm});
            skPoint(sketch, "E412.MirrorP", {"position": v(-11.3, -6.35) * mm});
            skLineSegment(sketch, "E413.MirrorCS", {"start": v(-43.04, -6.94) * mm, "end": v(-43.66, -9.62) * mm});
            skPoint(sketch, "E414.MirrorP", {"position": v(-31.52, -13.14) * mm});
            skLineSegment(sketch, "E415.MirrorCS", {"start": v(-28.88, -9.69) * mm, "end": v(-31.42, -9.6) * mm});
            skPoint(sketch, "E416.MirrorP", {"position": v(6.7, 11.69) * mm});
            skLineSegment(sketch, "E417.MirrorCS", {"start": v(-49.99, -1.98) * mm, "end": v(-51.86, -0.27) * mm});
            skLineSegment(sketch, "E418.MirrorCS", {"start": v(-60.3, 9.12) * mm, "end": v(-62.46, 7.29) * mm});
            skPoint(sketch, "E419.MirrorP", {"position": v(-47.53, -8.14) * mm});
            skPoint(sketch, "E420.MirrorP", {"position": v(-6.67, -8.14) * mm});
            skPoint(sketch, "E421.MirrorP", {"position": v(-49.54, -2.39) * mm});
            skPoint(sketch, "E422.MirrorP", {"position": v(-33.6, -9.31) * mm});
            skPoint(sketch, "E423.MirrorP", {"position": v(13.04, 19.5) * mm});
            skPoint(sketch, "E424.MirrorP", {"position": v(-44.96, -5.37) * mm});
            skLineSegment(sketch, "E425.MirrorCS", {"start": v(-64.13, 10.82) * mm, "end": v(-61.49, 11.53) * mm});
            skPoint(sketch, "E426.MirrorP", {"position": v(8.58, 7) * mm});
            skLineSegment(sketch, "E427.MirrorCS", {"start": v(-37.27, -8.95) * mm, "end": v(-37.5, -11.68) * mm});
            skPoint(sketch, "E428.MirrorP", {"position": v(-22.68, -13.14) * mm});
            skPoint(sketch, "E429.MirrorP", {"position": v(-16.66, -12.1) * mm});
            skPoint(sketch, "E430.MirrorP", {"position": v(-4.62, -6.81) * mm});
            skPoint(sketch, "E431.MirrorP", {"position": v(0.03, -2.89) * mm});
            skPoint(sketch, "E432.MirrorP", {"position": v(-64.9, 17.22) * mm});
            skLineSegment(sketch, "E433.MirrorCS", {"start": v(-28.93, -12.8) * mm, "end": v(-28.4, -10.3) * mm});
            skPoint(sketch, "E434.MirrorP", {"position": v(-1.82, -4.58) * mm});
            skLineSegment(sketch, "E435.MirrorCS", {"start": v(-31.94, -10.18) * mm, "end": v(-31.58, -12.72) * mm});
            skLineSegment(sketch, "E436.MirrorCS", {"start": v(-19.2, -12.35) * mm, "end": v(-20.35, -9.86) * mm});
            skPoint(sketch, "E437.MirrorP", {"position": v(-62.78, 7) * mm});
            skPoint(sketch, "E438.MirrorP", {"position": v(-32.02, -9.58) * mm});
            skPoint(sketch, "E439.MirrorP", {"position": v(-61.57, 4.93) * mm});
            skPoint(sketch, "E440.MirrorP", {"position": v(-67.24, 19.5) * mm});
            skPoint(sketch, "E441.MirrorP", {"position": v(-64.55, 10.71) * mm});
            skPoint(sketch, "E442.MirrorP", {"position": v(-59.83, 9.51) * mm});
            skPoint(sketch, "E443.MirrorP", {"position": v(-1.9, 0.14) * mm});
            skPoint(sketch, "E444.MirrorP", {"position": v(12.4, 17.07) * mm});
            skPoint(sketch, "E445.MirrorP", {"position": v(8.82, 17.38) * mm});
            skPoint(sketch, "E446.MirrorP", {"position": v(-0.07, 1.8) * mm});
            skPoint(sketch, "E447.MirrorP", {"position": v(-49.58, -6.81) * mm});
            skPoint(sketch, "E448.MirrorP", {"position": v(-42.9, -6.35) * mm});
            skLineSegment(sketch, "E449.MirrorCS", {"start": v(-61.16, 12.24) * mm, "end": v(-62.23, 14.54) * mm});
            skLineSegment(sketch, "E450.MirrorCS", {"start": v(-41.28, -10.63) * mm, "end": v(-39.78, -8.32) * mm});
            skPoint(sketch, "E451.MirrorP", {"position": v(-35.18, -12.73) * mm});
            skPoint(sketch, "E452.MirrorP", {"position": v(11.38, 12.92) * mm});
            skPoint(sketch, "E453.MirrorP", {"position": v(-48.12, -3.34) * mm});
            skPoint(sketch, "E454.MirrorP", {"position": v(4.76, 1.56) * mm});
            skLineSegment(sketch, "E455.MirrorCS", {"start": v(-58.25, 6.8) * mm, "end": v(-59.53, 8.99) * mm});
            skPoint(sketch, "E456.MirrorP", {"position": v(-39.45, -7.8) * mm});
            skPoint(sketch, "E457.MirrorP", {"position": v(9.79, 21) * mm});
            skPoint(sketch, "E458.MirrorP", {"position": v(-66.6, 17.07) * mm});
            skPoint(sketch, "E459.MirrorP", {"position": v(-12.69, -10.99) * mm});
            skPoint(sketch, "E460.MirrorP", {"position": v(-54.23, -2.89) * mm});
            skPoint(sketch, "E461.MirrorP", {"position": v(-19.02, -12.73) * mm});
            skLineSegment(sketch, "E462.MirrorCS", {"start": v(-64.54, 20.75) * mm, "end": v(-66.86, 19.67) * mm});
            skPoint(sketch, "E463.MirrorP", {"position": v(-37.22, -8.34) * mm});
            skLineSegment(sketch, "E464.MirrorCS", {"start": v(-34.18, -9.15) * mm, "end": v(-36.63, -8.5) * mm});
            skPoint(sketch, "E465.MirrorP", {"position": v(-58.96, 1.56) * mm});
            skPoint(sketch, "E466.MirrorP", {"position": v(-29.02, -13.22) * mm});
            skPoint(sketch, "E467.MirrorP", {"position": v(-14.75, -7.8) * mm});
            skPoint(sketch, "E468.MirrorP", {"position": v(-52.38, -4.58) * mm});
            skLineSegment(sketch, "E469.MirrorCS", {"start": v(-52.63, -0.37) * mm, "end": v(-54, -2.53) * mm});
            skPoint(sketch, "E470.MirrorP", {"position": v(8.29, 15.09) * mm});
            skLineSegment(sketch, "E471.MirrorCS", {"start": v(-47.24, -7.82) * mm, "end": v(-45.38, -5.81) * mm});
            skPoint(sketch, "E472.MirrorP", {"position": v(-37.54, -12.1) * mm});
            skPoint(sketch, "E473.MirrorP", {"position": v(-65.58, 12.92) * mm});
            skPoint(sketch, "E474.MirrorP", {"position": v(10.7, 17.22) * mm});
            skLineSegment(sketch, "E475.MirrorCS", {"start": v(-56.95, 0) * mm, "end": v(-54.64, 1.48) * mm});
            skPoint(sketch, "E476.MirrorP", {"position": v(10.34, 10.71) * mm});
            skLineSegment(sketch, "E477.MirrorCS", {"start": v(-35, -12.35) * mm, "end": v(-33.85, -9.86) * mm});
            skPoint(sketch, "E478.MirrorP", {"position": v(3.74, 6.27) * mm});
            skLineSegment(sketch, "E479.MirrorCS", {"start": v(-67.53, 23.07) * mm, "end": v(-64.8, 22.72) * mm});
            skPoint(sketch, "E480.MirrorP", {"position": v(-62.49, 15.09) * mm});
            skPoint(sketch, "E481.MirrorP", {"position": v(-57.3, -0.23) * mm});
            skPoint(sketch, "E482.MirrorP", {"position": v(-68.06, 25.56) * mm});
            skPoint(sketch, "E483.MirrorP", {"position": v(13.86, 25.56) * mm});
            skPoint(sketch, "E484.MirrorP", {"position": v(13.75, 23.12) * mm});
            skPoint(sketch, "E485.MirrorP", {"position": v(-67.95, 23.12) * mm});
            skSolve(sketch);
        }
        {
            var Q0;
            Q0=qCreatedBy(makeId("Front.planeOp"),FACE);
            var sketch = newSketch(context, id + "F1", { "sketchPlane" : qUnion([Q0])});
            skCircle(sketch, "E486", {"center": v(23.04, -32.45) * mm, "radius": 19.05 * mm});
            skCircle(sketch, "E487", {"center": v(23.04, -32.45) * mm, "radius": 6.35 * mm});
            skLineSegment(sketch, "E488", {"start": v(23.04, -13.4) * mm, "end": v(23.04, -51.5) * mm, "construction": true});
            skLineSegment(sketch, "E489", {"start": v(4, -32.45) * mm, "end": v(42.1, -32.45) * mm, "construction": true});
            skLineSegment(sketch, "E490", {"start": v(41.13, -28.9) * mm, "end": v(41.3, -30.83) * mm});
            skLineSegment(sketch, "E491", {"start": v(44.41, -28.59) * mm, "end": v(41.68, -28.35) * mm});
            skLineSegment(sketch, "E492", {"start": v(41.94, -31.28) * mm, "end": v(44.59, -30.57) * mm});
            skLineSegment(sketch, "E493", {"start": v(44.88, -29.05) * mm, "end": v(44.96, -30.03) * mm});
            skPoint(sketch, "E494.visualSharp", {"position": v(44.84, -28.63) * mm});
            skArc(sketch, "E494.filletArc", {"start": v(44.88, -29.05) * mm, "mid": v(44.73, -28.74) * mm, "end": v(44.41, -28.59) * mm});
            skPoint(sketch, "E495.visualSharp", {"position": v(41.08, -28.3) * mm});
            skArc(sketch, "E495.filletArc", {"start": v(41.68, -28.35) * mm, "mid": v(41.28, -28.5) * mm, "end": v(41.13, -28.9) * mm});
            skPoint(sketch, "E496.visualSharp", {"position": v(41.35, -31.43) * mm});
            skArc(sketch, "E496.filletArc", {"start": v(41.3, -30.83) * mm, "mid": v(41.52, -31.2) * mm, "end": v(41.94, -31.28) * mm});
            skPoint(sketch, "E497.visualSharp", {"position": v(45, -30.46) * mm});
            skArc(sketch, "E497.filletArc", {"start": v(44.59, -30.57) * mm, "mid": v(44.87, -30.37) * mm, "end": v(44.96, -30.03) * mm});
            skLineSegment(sketch, "E498.0", {"start": v(45, -30.46) * mm, "end": v(44.84, -28.63) * mm, "construction": true});
            skLineSegment(sketch, "E499", {"start": v(38.78, -23.42) * mm, "end": v(39.73, -25.1) * mm});
            skLineSegment(sketch, "E500", {"start": v(41.64, -21.78) * mm, "end": v(39.05, -22.69) * mm});
            skLineSegment(sketch, "E501", {"start": v(40.5, -25.25) * mm, "end": v(42.61, -23.51) * mm});
            skLineSegment(sketch, "E502", {"start": v(42.25, -22.01) * mm, "end": v(42.73, -22.87) * mm});
            skPoint(sketch, "E503.visualSharp", {"position": v(42.04, -21.64) * mm});
            skArc(sketch, "E503.filletArc", {"start": v(42.25, -22.01) * mm, "mid": v(41.99, -21.78) * mm, "end": v(41.64, -21.78) * mm});
            skPoint(sketch, "E504.visualSharp", {"position": v(38.48, -22.89) * mm});
            skArc(sketch, "E504.filletArc", {"start": v(39.05, -22.69) * mm, "mid": v(38.75, -22.99) * mm, "end": v(38.78, -23.42) * mm});
            skPoint(sketch, "E505.visualSharp", {"position": v(40.02, -25.63) * mm});
            skArc(sketch, "E505.filletArc", {"start": v(39.73, -25.1) * mm, "mid": v(40.08, -25.36) * mm, "end": v(40.5, -25.25) * mm});
            skPoint(sketch, "E506.visualSharp", {"position": v(42.94, -23.24) * mm});
            skArc(sketch, "E506.filletArc", {"start": v(42.61, -23.51) * mm, "mid": v(42.8, -23.21) * mm, "end": v(42.73, -22.87) * mm});
            skLineSegment(sketch, "E507.0", {"start": v(42.94, -23.24) * mm, "end": v(42.04, -21.64) * mm, "construction": true});
            skLineSegment(sketch, "E508", {"start": v(35.02, -18.63) * mm, "end": v(36.4, -20) * mm});
            skLineSegment(sketch, "E509", {"start": v(37.34, -16.28) * mm, "end": v(35.1, -17.86) * mm});
            skLineSegment(sketch, "E510", {"start": v(37.17, -19.94) * mm, "end": v(38.74, -17.69) * mm});
            skLineSegment(sketch, "E511", {"start": v(37.99, -16.34) * mm, "end": v(38.69, -17.04) * mm});
            skPoint(sketch, "E512.visualSharp", {"position": v(37.69, -16.04) * mm});
            skArc(sketch, "E512.filletArc", {"start": v(37.99, -16.34) * mm, "mid": v(37.67, -16.2) * mm, "end": v(37.34, -16.28) * mm});
            skPoint(sketch, "E513.visualSharp", {"position": v(34.6, -18.2) * mm});
            skArc(sketch, "E513.filletArc", {"start": v(35.1, -17.86) * mm, "mid": v(34.88, -18.23) * mm, "end": v(35.02, -18.63) * mm});
            skPoint(sketch, "E514.visualSharp", {"position": v(36.82, -20.43) * mm});
            skArc(sketch, "E514.filletArc", {"start": v(36.4, -20) * mm, "mid": v(36.8, -20.15) * mm, "end": v(37.17, -19.94) * mm});
            skPoint(sketch, "E515.visualSharp", {"position": v(38.99, -17.34) * mm});
            skArc(sketch, "E515.filletArc", {"start": v(38.74, -17.69) * mm, "mid": v(38.83, -17.35) * mm, "end": v(38.69, -17.04) * mm});
            skLineSegment(sketch, "E516.0", {"start": v(38.99, -17.34) * mm, "end": v(37.69, -16.04) * mm, "construction": true});
            skLineSegment(sketch, "E517", {"start": v(30.44, -15.62) * mm, "end": v(32.12, -16.6) * mm});
            skLineSegment(sketch, "E518", {"start": v(32.07, -12.76) * mm, "end": v(30.3, -14.86) * mm});
            skLineSegment(sketch, "E519", {"start": v(32.85, -16.33) * mm, "end": v(33.79, -13.75) * mm});
            skLineSegment(sketch, "E520", {"start": v(32.71, -12.64) * mm, "end": v(33.57, -13.14) * mm});
            skPoint(sketch, "E521.visualSharp", {"position": v(32.34, -12.43) * mm});
            skArc(sketch, "E521.filletArc", {"start": v(32.71, -12.64) * mm, "mid": v(32.37, -12.58) * mm, "end": v(32.07, -12.76) * mm});
            skPoint(sketch, "E522.visualSharp", {"position": v(29.92, -15.32) * mm});
            skArc(sketch, "E522.filletArc", {"start": v(30.3, -14.86) * mm, "mid": v(30.2, -15.27) * mm, "end": v(30.44, -15.62) * mm});
            skPoint(sketch, "E523.visualSharp", {"position": v(32.65, -16.9) * mm});
            skArc(sketch, "E523.filletArc", {"start": v(32.12, -16.6) * mm, "mid": v(32.55, -16.63) * mm, "end": v(32.85, -16.33) * mm});
            skPoint(sketch, "E524.visualSharp", {"position": v(33.94, -13.35) * mm});
            skArc(sketch, "E524.filletArc", {"start": v(33.79, -13.75) * mm, "mid": v(33.79, -13.4) * mm, "end": v(33.57, -13.14) * mm});
            skLineSegment(sketch, "E525.0", {"start": v(33.94, -13.35) * mm, "end": v(32.34, -12.43) * mm, "construction": true});
            skLineSegment(sketch, "E526", {"start": v(24.93, -14.08) * mm, "end": v(26.84, -14.42) * mm});
            skLineSegment(sketch, "E527", {"start": v(25.47, -10.83) * mm, "end": v(24.54, -13.41) * mm});
            skLineSegment(sketch, "E528", {"start": v(27.43, -13.92) * mm, "end": v(27.43, -11.18) * mm});
            skLineSegment(sketch, "E529", {"start": v(26.04, -10.5) * mm, "end": v(27.01, -10.68) * mm});
            skPoint(sketch, "E530.visualSharp", {"position": v(25.62, -10.43) * mm});
            skArc(sketch, "E530.filletArc", {"start": v(26.04, -10.5) * mm, "mid": v(25.7, -10.57) * mm, "end": v(25.47, -10.83) * mm});
            skPoint(sketch, "E531.visualSharp", {"position": v(24.33, -13.98) * mm});
            skArc(sketch, "E531.filletArc", {"start": v(24.54, -13.41) * mm, "mid": v(24.57, -13.84) * mm, "end": v(24.93, -14.08) * mm});
            skPoint(sketch, "E532.visualSharp", {"position": v(27.43, -14.53) * mm});
            skArc(sketch, "E532.filletArc", {"start": v(26.84, -14.42) * mm, "mid": v(27.25, -14.31) * mm, "end": v(27.43, -13.92) * mm});
            skPoint(sketch, "E533.visualSharp", {"position": v(27.43, -10.75) * mm});
            skArc(sketch, "E533.filletArc", {"start": v(27.43, -11.18) * mm, "mid": v(27.31, -10.85) * mm, "end": v(27.01, -10.68) * mm});
            skLineSegment(sketch, "E534.0", {"start": v(27.43, -10.75) * mm, "end": v(25.62, -10.43) * mm, "construction": true});
            skLineSegment(sketch, "E535.MirrorCS", {"start": v(20.05, -10.5) * mm, "end": v(19.08, -10.68) * mm});
            skArc(sketch, "E536.MirrorCS", {"start": v(20.05, -10.5) * mm, "mid": v(20.4, -10.57) * mm, "end": v(20.61, -10.83) * mm});
            skLineSegment(sketch, "E537.MirrorCS", {"start": v(1.09, -30.46) * mm, "end": v(1.25, -28.63) * mm, "construction": true});
            skArc(sketch, "E538.MirrorCS", {"start": v(18.66, -11.18) * mm, "mid": v(18.78, -10.85) * mm, "end": v(19.08, -10.68) * mm});
            skLineSegment(sketch, "E539.MirrorCS", {"start": v(1.21, -29.05) * mm, "end": v(1.13, -30.03) * mm});
            skArc(sketch, "E540.MirrorCS", {"start": v(13.38, -12.64) * mm, "mid": v(13.72, -12.58) * mm, "end": v(14.02, -12.76) * mm});
            skArc(sketch, "E541.MirrorCS", {"start": v(11, -17.86) * mm, "mid": v(11.21, -18.23) * mm, "end": v(11.06, -18.63) * mm});
            skArc(sketch, "E542.MirrorCS", {"start": v(6.36, -25.1) * mm, "mid": v(6.01, -25.36) * mm, "end": v(5.6, -25.25) * mm});
            skArc(sketch, "E543.MirrorCS", {"start": v(8.1, -16.34) * mm, "mid": v(8.41, -16.2) * mm, "end": v(8.75, -16.28) * mm});
            skLineSegment(sketch, "E544.MirrorCS", {"start": v(13.38, -12.64) * mm, "end": v(12.52, -13.14) * mm});
            skArc(sketch, "E545.MirrorCS", {"start": v(7.35, -17.69) * mm, "mid": v(7.26, -17.35) * mm, "end": v(7.4, -17.04) * mm});
            skArc(sketch, "E546.MirrorCS", {"start": v(3.48, -23.51) * mm, "mid": v(3.3, -23.21) * mm, "end": v(3.35, -22.87) * mm});
            skArc(sketch, "E547.MirrorCS", {"start": v(13.97, -16.6) * mm, "mid": v(13.54, -16.63) * mm, "end": v(13.24, -16.33) * mm});
            skArc(sketch, "E548.MirrorCS", {"start": v(15.78, -14.86) * mm, "mid": v(15.9, -15.27) * mm, "end": v(15.65, -15.62) * mm});
            skArc(sketch, "E549.MirrorCS", {"start": v(9.7, -20) * mm, "mid": v(9.29, -20.15) * mm, "end": v(8.92, -19.94) * mm});
            skArc(sketch, "E550.MirrorCS", {"start": v(7.04, -22.69) * mm, "mid": v(7.34, -22.99) * mm, "end": v(7.31, -23.42) * mm});
            skLineSegment(sketch, "E551.MirrorCS", {"start": v(8.1, -16.34) * mm, "end": v(7.4, -17.04) * mm});
            skArc(sketch, "E552.MirrorCS", {"start": v(1.5, -30.57) * mm, "mid": v(1.22, -30.37) * mm, "end": v(1.13, -30.03) * mm});
            skLineSegment(sketch, "E553.MirrorCS", {"start": v(7.1, -17.34) * mm, "end": v(8.4, -16.04) * mm, "construction": true});
            skLineSegment(sketch, "E554.MirrorCS", {"start": v(18.66, -10.75) * mm, "end": v(20.47, -10.43) * mm, "construction": true});
            skArc(sketch, "E555.MirrorCS", {"start": v(3.84, -22.01) * mm, "mid": v(4.1, -21.78) * mm, "end": v(4.45, -21.78) * mm});
            skArc(sketch, "E556.MirrorCS", {"start": v(12.3, -13.75) * mm, "mid": v(12.3, -13.4) * mm, "end": v(12.52, -13.14) * mm});
            skArc(sketch, "E557.MirrorCS", {"start": v(21.55, -13.41) * mm, "mid": v(21.51, -13.84) * mm, "end": v(21.16, -14.08) * mm});
            skLineSegment(sketch, "E558.MirrorCS", {"start": v(3.84, -22.01) * mm, "end": v(3.35, -22.87) * mm});
            skArc(sketch, "E559.MirrorCS", {"start": v(4.79, -30.83) * mm, "mid": v(4.57, -31.2) * mm, "end": v(4.15, -31.28) * mm});
            skLineSegment(sketch, "E560.MirrorCS", {"start": v(3.15, -23.24) * mm, "end": v(4.05, -21.64) * mm, "construction": true});
            skLineSegment(sketch, "E561.MirrorCS", {"start": v(12.15, -13.35) * mm, "end": v(13.75, -12.43) * mm, "construction": true});
            skArc(sketch, "E562.MirrorCS", {"start": v(19.25, -14.42) * mm, "mid": v(18.84, -14.31) * mm, "end": v(18.66, -13.92) * mm});
            skArc(sketch, "E563.MirrorCS", {"start": v(1.21, -29.05) * mm, "mid": v(1.36, -28.74) * mm, "end": v(1.67, -28.59) * mm});
            skArc(sketch, "E564.MirrorCS", {"start": v(4.4, -28.35) * mm, "mid": v(4.8, -28.5) * mm, "end": v(4.96, -28.9) * mm});
            skPoint(sketch, "E565.MirrorP", {"position": v(4.73, -31.43) * mm});
            skPoint(sketch, "E566.MirrorP", {"position": v(9.27, -20.43) * mm});
            skPoint(sketch, "E567.MirrorP", {"position": v(13.44, -16.9) * mm});
            skPoint(sketch, "E568.MirrorP", {"position": v(21.76, -13.98) * mm});
            skPoint(sketch, "E569.MirrorP", {"position": v(7.6, -22.89) * mm});
            skPoint(sketch, "E570.MirrorP", {"position": v(3.15, -23.24) * mm});
            skPoint(sketch, "E571.MirrorP", {"position": v(18.66, -10.75) * mm});
            skLineSegment(sketch, "E572.MirrorCS", {"start": v(15.65, -15.62) * mm, "end": v(13.97, -16.6) * mm});
            skLineSegment(sketch, "E573.MirrorCS", {"start": v(18.66, -13.92) * mm, "end": v(18.66, -11.18) * mm});
            skLineSegment(sketch, "E574.MirrorCS", {"start": v(13.24, -16.33) * mm, "end": v(12.3, -13.75) * mm});
            skLineSegment(sketch, "E575.MirrorCS", {"start": v(8.75, -16.28) * mm, "end": v(11, -17.86) * mm});
            skLineSegment(sketch, "E576.MirrorCS", {"start": v(14.02, -12.76) * mm, "end": v(15.78, -14.86) * mm});
            skLineSegment(sketch, "E577.MirrorCS", {"start": v(5.6, -25.25) * mm, "end": v(3.48, -23.51) * mm});
            skLineSegment(sketch, "E578.MirrorCS", {"start": v(8.92, -19.94) * mm, "end": v(7.35, -17.69) * mm});
            skPoint(sketch, "E579.MirrorP", {"position": v(1.09, -30.46) * mm});
            skPoint(sketch, "E580.MirrorP", {"position": v(7.1, -17.34) * mm});
            skLineSegment(sketch, "E581.MirrorCS", {"start": v(4.45, -21.78) * mm, "end": v(7.04, -22.69) * mm});
            skPoint(sketch, "E582.MirrorP", {"position": v(12.15, -13.35) * mm});
            skPoint(sketch, "E583.MirrorP", {"position": v(20.47, -10.43) * mm});
            skLineSegment(sketch, "E584.MirrorCS", {"start": v(7.31, -23.42) * mm, "end": v(6.36, -25.1) * mm});
            skLineSegment(sketch, "E585.MirrorCS", {"start": v(1.67, -28.59) * mm, "end": v(4.4, -28.35) * mm});
            skLineSegment(sketch, "E586.MirrorCS", {"start": v(4.96, -28.9) * mm, "end": v(4.79, -30.83) * mm});
            skLineSegment(sketch, "E587.MirrorCS", {"start": v(4.15, -31.28) * mm, "end": v(1.5, -30.57) * mm});
            skPoint(sketch, "E588.MirrorP", {"position": v(18.66, -14.53) * mm});
            skPoint(sketch, "E589.MirrorP", {"position": v(4.05, -21.64) * mm});
            skLineSegment(sketch, "E590.MirrorCS", {"start": v(11.06, -18.63) * mm, "end": v(9.7, -20) * mm});
            skPoint(sketch, "E591.MirrorP", {"position": v(6.06, -25.63) * mm});
            skPoint(sketch, "E592.MirrorP", {"position": v(13.75, -12.43) * mm});
            skLineSegment(sketch, "E593.MirrorCS", {"start": v(21.16, -14.08) * mm, "end": v(19.25, -14.42) * mm});
            skLineSegment(sketch, "E594.MirrorCS", {"start": v(20.61, -10.83) * mm, "end": v(21.55, -13.41) * mm});
            skPoint(sketch, "E595.MirrorP", {"position": v(5, -28.3) * mm});
            skPoint(sketch, "E596.MirrorP", {"position": v(11.5, -18.2) * mm});
            skPoint(sketch, "E597.MirrorP", {"position": v(16.17, -15.32) * mm});
            skPoint(sketch, "E598.MirrorP", {"position": v(1.25, -28.63) * mm});
            skPoint(sketch, "E599.MirrorP", {"position": v(8.4, -16.04) * mm});
            skLineSegment(sketch, "E600.MirrorCS", {"start": v(42.25, -42.88) * mm, "end": v(42.73, -42.02) * mm});
            skArc(sketch, "E601.MirrorCS", {"start": v(37.99, -48.55) * mm, "mid": v(37.67, -48.7) * mm, "end": v(37.34, -48.6) * mm});
            skLineSegment(sketch, "E602.MirrorCS", {"start": v(32.71, -52.25) * mm, "end": v(33.57, -51.76) * mm});
            skArc(sketch, "E603.MirrorCS", {"start": v(20.05, -54.39) * mm, "mid": v(20.4, -54.32) * mm, "end": v(20.61, -54.06) * mm});
            skArc(sketch, "E604.MirrorCS", {"start": v(2, -35.52) * mm, "mid": v(1.73, -35.75) * mm, "end": v(1.67, -36.09) * mm});
            skLineSegment(sketch, "E605.MirrorCS", {"start": v(37.99, -48.55) * mm, "end": v(38.69, -47.85) * mm});
            skLineSegment(sketch, "E606.MirrorCS", {"start": v(8.1, -48.55) * mm, "end": v(7.4, -47.85) * mm});
            skArc(sketch, "E607.MirrorCS", {"start": v(44.7, -35.1) * mm, "mid": v(44.97, -35.31) * mm, "end": v(45.04, -35.65) * mm});
            skArc(sketch, "E608.MirrorCS", {"start": v(41.42, -34.68) * mm, "mid": v(41.65, -34.32) * mm, "end": v(42.08, -34.27) * mm});
            skArc(sketch, "E609.MirrorCS", {"start": v(41.68, -37.18) * mm, "mid": v(41.29, -37.02) * mm, "end": v(41.16, -36.6) * mm});
            skArc(sketch, "E610.MirrorCS", {"start": v(44.9, -36.63) * mm, "mid": v(44.75, -36.94) * mm, "end": v(44.42, -37.07) * mm});
            skLineSegment(sketch, "E611.MirrorCS", {"start": v(44.9, -36.63) * mm, "end": v(45.04, -35.65) * mm});
            skArc(sketch, "E612.MirrorCS", {"start": v(7.04, -42.2) * mm, "mid": v(7.34, -41.9) * mm, "end": v(7.31, -41.48) * mm});
            skArc(sketch, "E613.MirrorCS", {"start": v(27.43, -53.71) * mm, "mid": v(27.31, -54.04) * mm, "end": v(27.01, -54.21) * mm});
            skArc(sketch, "E614.MirrorCS", {"start": v(9.7, -44.89) * mm, "mid": v(9.29, -44.74) * mm, "end": v(8.92, -44.96) * mm});
            skArc(sketch, "E615.MirrorCS", {"start": v(26.84, -50.47) * mm, "mid": v(27.25, -50.58) * mm, "end": v(27.43, -50.97) * mm});
            skArc(sketch, "E616.MirrorCS", {"start": v(15.78, -50.03) * mm, "mid": v(15.9, -49.62) * mm, "end": v(15.65, -49.27) * mm});
            skArc(sketch, "E617.MirrorCS", {"start": v(5.08, -37.48) * mm, "mid": v(5.47, -37.3) * mm, "end": v(5.58, -36.88) * mm});
            skArc(sketch, "E618.MirrorCS", {"start": v(24.54, -51.48) * mm, "mid": v(24.57, -51.05) * mm, "end": v(24.93, -50.8) * mm});
            skArc(sketch, "E619.MirrorCS", {"start": v(13.97, -48.3) * mm, "mid": v(13.54, -48.26) * mm, "end": v(13.24, -48.57) * mm});
            skArc(sketch, "E620.MirrorCS", {"start": v(1.84, -37.06) * mm, "mid": v(2.01, -37.36) * mm, "end": v(2.34, -37.48) * mm});
            skLineSegment(sketch, "E621.MirrorCS", {"start": v(42.94, -41.65) * mm, "end": v(42.04, -43.25) * mm, "construction": true});
            skLineSegment(sketch, "E622.MirrorCS", {"start": v(7.1, -47.55) * mm, "end": v(8.4, -48.85) * mm, "construction": true});
            skArc(sketch, "E623.MirrorCS", {"start": v(32.71, -52.25) * mm, "mid": v(32.37, -52.3) * mm, "end": v(32.07, -52.13) * mm});
            skArc(sketch, "E624.MirrorCS", {"start": v(35.1, -47.04) * mm, "mid": v(34.88, -46.66) * mm, "end": v(35.02, -46.26) * mm});
            skArc(sketch, "E625.MirrorCS", {"start": v(38.74, -47.2) * mm, "mid": v(38.83, -47.54) * mm, "end": v(38.69, -47.85) * mm});
            skArc(sketch, "E626.MirrorCS", {"start": v(3.84, -42.88) * mm, "mid": v(4.1, -43.1) * mm, "end": v(4.45, -43.11) * mm});
            skArc(sketch, "E627.MirrorCS", {"start": v(32.12, -48.3) * mm, "mid": v(32.55, -48.26) * mm, "end": v(32.85, -48.57) * mm});
            skArc(sketch, "E628.MirrorCS", {"start": v(42.25, -42.88) * mm, "mid": v(41.99, -43.1) * mm, "end": v(41.64, -43.11) * mm});
            skArc(sketch, "E629.MirrorCS", {"start": v(8.1, -48.55) * mm, "mid": v(8.41, -48.7) * mm, "end": v(8.75, -48.6) * mm});
            skArc(sketch, "E630.MirrorCS", {"start": v(26.04, -54.39) * mm, "mid": v(25.7, -54.32) * mm, "end": v(25.47, -54.06) * mm});
            skArc(sketch, "E631.MirrorCS", {"start": v(3.48, -41.38) * mm, "mid": v(3.3, -41.68) * mm, "end": v(3.35, -42.02) * mm});
            skArc(sketch, "E632.MirrorCS", {"start": v(42.61, -41.38) * mm, "mid": v(42.8, -41.68) * mm, "end": v(42.73, -42.02) * mm});
            skArc(sketch, "E633.MirrorCS", {"start": v(5.24, -34.97) * mm, "mid": v(5, -34.62) * mm, "end": v(4.57, -34.58) * mm});
            skArc(sketch, "E634.MirrorCS", {"start": v(39.05, -42.2) * mm, "mid": v(38.75, -41.9) * mm, "end": v(38.78, -41.48) * mm});
            skArc(sketch, "E635.MirrorCS", {"start": v(39.73, -39.79) * mm, "mid": v(40.08, -39.54) * mm, "end": v(40.5, -39.64) * mm});
            skLineSegment(sketch, "E636.MirrorCS", {"start": v(12.15, -51.54) * mm, "end": v(13.75, -52.46) * mm, "construction": true});
            skArc(sketch, "E637.MirrorCS", {"start": v(7.35, -47.2) * mm, "mid": v(7.26, -47.54) * mm, "end": v(7.4, -47.85) * mm});
            skLineSegment(sketch, "E638.MirrorCS", {"start": v(3.15, -41.65) * mm, "end": v(4.05, -43.25) * mm, "construction": true});
            skLineSegment(sketch, "E639.MirrorCS", {"start": v(13.38, -52.25) * mm, "end": v(12.52, -51.76) * mm});
            skArc(sketch, "E640.MirrorCS", {"start": v(13.38, -52.25) * mm, "mid": v(13.72, -52.3) * mm, "end": v(14.02, -52.13) * mm});
            skArc(sketch, "E641.MirrorCS", {"start": v(12.3, -51.14) * mm, "mid": v(12.3, -51.49) * mm, "end": v(12.52, -51.76) * mm});
            skArc(sketch, "E642.MirrorCS", {"start": v(6.36, -39.79) * mm, "mid": v(6.01, -39.54) * mm, "end": v(5.6, -39.64) * mm});
            skArc(sketch, "E643.MirrorCS", {"start": v(33.79, -51.14) * mm, "mid": v(33.79, -51.49) * mm, "end": v(33.57, -51.76) * mm});
            skArc(sketch, "E644.MirrorCS", {"start": v(18.66, -53.71) * mm, "mid": v(18.78, -54.04) * mm, "end": v(19.08, -54.21) * mm});
            skArc(sketch, "E645.MirrorCS", {"start": v(21.55, -51.48) * mm, "mid": v(21.51, -51.05) * mm, "end": v(21.16, -50.8) * mm});
            skLineSegment(sketch, "E646.MirrorCS", {"start": v(26.04, -54.39) * mm, "end": v(27.01, -54.21) * mm});
            skArc(sketch, "E647.MirrorCS", {"start": v(36.4, -44.89) * mm, "mid": v(36.8, -44.74) * mm, "end": v(37.17, -44.96) * mm});
            skLineSegment(sketch, "E648.MirrorCS", {"start": v(3.84, -42.88) * mm, "end": v(3.35, -42.02) * mm});
            skArc(sketch, "E649.MirrorCS", {"start": v(30.3, -50.03) * mm, "mid": v(30.2, -49.62) * mm, "end": v(30.44, -49.27) * mm});
            skLineSegment(sketch, "E650.MirrorCS", {"start": v(38.99, -47.55) * mm, "end": v(37.69, -48.85) * mm, "construction": true});
            skArc(sketch, "E651.MirrorCS", {"start": v(11, -47.04) * mm, "mid": v(11.21, -46.66) * mm, "end": v(11.06, -46.26) * mm});
            skLineSegment(sketch, "E652.MirrorCS", {"start": v(33.94, -51.54) * mm, "end": v(32.34, -52.46) * mm, "construction": true});
            skLineSegment(sketch, "E653.MirrorCS", {"start": v(45.1, -35.23) * mm, "end": v(44.85, -37.05) * mm, "construction": true});
            skLineSegment(sketch, "E654.MirrorCS", {"start": v(20.05, -54.39) * mm, "end": v(19.08, -54.21) * mm});
            skLineSegment(sketch, "E655.MirrorCS", {"start": v(27.43, -54.14) * mm, "end": v(25.62, -54.46) * mm, "construction": true});
            skLineSegment(sketch, "E656.MirrorCS", {"start": v(1.84, -37.06) * mm, "end": v(1.67, -36.09) * mm});
            skArc(sketch, "E657.MirrorCS", {"start": v(19.25, -50.47) * mm, "mid": v(18.84, -50.58) * mm, "end": v(18.66, -50.97) * mm});
            skPoint(sketch, "E658.MirrorP", {"position": v(44.85, -37.05) * mm});
            skPoint(sketch, "E659.MirrorP", {"position": v(37.69, -48.85) * mm});
            skPoint(sketch, "E660.MirrorP", {"position": v(32.34, -52.46) * mm});
            skLineSegment(sketch, "E661.MirrorCS", {"start": v(8.75, -48.6) * mm, "end": v(11, -47.04) * mm});
            skPoint(sketch, "E662.MirrorP", {"position": v(4.05, -43.25) * mm});
            skLineSegment(sketch, "E663.MirrorCS", {"start": v(13.24, -48.57) * mm, "end": v(12.3, -51.14) * mm});
            skLineSegment(sketch, "E664.MirrorCS", {"start": v(32.85, -48.57) * mm, "end": v(33.79, -51.14) * mm});
            skPoint(sketch, "E665.MirrorP", {"position": v(18.66, -50.37) * mm});
            skLineSegment(sketch, "E666.MirrorCS", {"start": v(42.08, -34.27) * mm, "end": v(44.7, -35.1) * mm});
            skLineSegment(sketch, "E667.MirrorCS", {"start": v(44.42, -37.07) * mm, "end": v(41.68, -37.18) * mm});
            skLineSegment(sketch, "E668.MirrorCS", {"start": v(41.16, -36.6) * mm, "end": v(41.42, -34.68) * mm});
            skLineSegment(sketch, "E669.MirrorCS", {"start": v(40.5, -39.64) * mm, "end": v(42.61, -41.38) * mm});
            skLineSegment(sketch, "E670.MirrorCS", {"start": v(41.64, -43.11) * mm, "end": v(39.05, -42.2) * mm});
            skLineSegment(sketch, "E671.MirrorCS", {"start": v(38.78, -41.48) * mm, "end": v(39.73, -39.79) * mm});
            skLineSegment(sketch, "E672.MirrorCS", {"start": v(18.66, -50.97) * mm, "end": v(18.66, -53.71) * mm});
            skLineSegment(sketch, "E673.MirrorCS", {"start": v(37.17, -44.96) * mm, "end": v(38.74, -47.2) * mm});
            skLineSegment(sketch, "E674.MirrorCS", {"start": v(32.07, -52.13) * mm, "end": v(30.3, -50.03) * mm});
            skPoint(sketch, "E675.MirrorP", {"position": v(20.47, -54.46) * mm});
            skPoint(sketch, "E676.MirrorP", {"position": v(42.94, -41.65) * mm});
            skPoint(sketch, "E677.MirrorP", {"position": v(27.43, -54.14) * mm});
            skLineSegment(sketch, "E678.MirrorCS", {"start": v(15.65, -49.27) * mm, "end": v(13.97, -48.3) * mm});
            skLineSegment(sketch, "E679.MirrorCS", {"start": v(37.34, -48.6) * mm, "end": v(35.1, -47.04) * mm});
            skLineSegment(sketch, "E680.MirrorCS", {"start": v(30.44, -49.27) * mm, "end": v(32.12, -48.3) * mm});
            skPoint(sketch, "E681.MirrorP", {"position": v(12.15, -51.54) * mm});
            skLineSegment(sketch, "E682.MirrorCS", {"start": v(35.02, -46.26) * mm, "end": v(36.4, -44.89) * mm});
            skPoint(sketch, "E683.MirrorP", {"position": v(27.43, -50.37) * mm});
            skPoint(sketch, "E684.MirrorP", {"position": v(7.1, -47.55) * mm});
            skPoint(sketch, "E685.MirrorP", {"position": v(40.02, -39.26) * mm});
            skLineSegment(sketch, "E686.MirrorCS", {"start": v(20.61, -54.06) * mm, "end": v(21.55, -51.48) * mm});
            skPoint(sketch, "E687.MirrorP", {"position": v(1.6, -35.67) * mm});
            skLineSegment(sketch, "E688.MirrorCS", {"start": v(1.6, -35.67) * mm, "end": v(1.91, -37.48) * mm, "construction": true});
            skLineSegment(sketch, "E689.MirrorCS", {"start": v(14.02, -52.13) * mm, "end": v(15.78, -50.03) * mm});
            skPoint(sketch, "E690.MirrorP", {"position": v(13.75, -52.46) * mm});
            skPoint(sketch, "E691.MirrorP", {"position": v(21.76, -50.91) * mm});
            skLineSegment(sketch, "E692.MirrorCS", {"start": v(8.92, -44.96) * mm, "end": v(7.35, -47.2) * mm});
            skPoint(sketch, "E693.MirrorP", {"position": v(1.91, -37.48) * mm});
            skPoint(sketch, "E694.MirrorP", {"position": v(16.17, -49.57) * mm});
            skLineSegment(sketch, "E695.MirrorCS", {"start": v(21.16, -50.8) * mm, "end": v(19.25, -50.47) * mm});
            skPoint(sketch, "E696.MirrorP", {"position": v(38.99, -47.55) * mm});
            skPoint(sketch, "E697.MirrorP", {"position": v(33.94, -51.54) * mm});
            skPoint(sketch, "E698.MirrorP", {"position": v(13.44, -48) * mm});
            skPoint(sketch, "E699.MirrorP", {"position": v(24.33, -50.91) * mm});
            skPoint(sketch, "E700.MirrorP", {"position": v(18.66, -54.14) * mm});
            skLineSegment(sketch, "E701.MirrorCS", {"start": v(5.58, -36.88) * mm, "end": v(5.24, -34.97) * mm});
            skLineSegment(sketch, "E702.MirrorCS", {"start": v(25.47, -54.06) * mm, "end": v(24.54, -51.48) * mm});
            skPoint(sketch, "E703.MirrorP", {"position": v(41.5, -34.08) * mm});
            skPoint(sketch, "E704.MirrorP", {"position": v(5.14, -34.38) * mm});
            skPoint(sketch, "E705.MirrorP", {"position": v(32.65, -48) * mm});
            skLineSegment(sketch, "E706.MirrorCS", {"start": v(4.57, -34.58) * mm, "end": v(2, -35.52) * mm});
            skPoint(sketch, "E707.MirrorP", {"position": v(9.27, -44.46) * mm});
            skPoint(sketch, "E708.MirrorP", {"position": v(42.04, -43.25) * mm});
            skPoint(sketch, "E709.MirrorP", {"position": v(34.6, -46.69) * mm});
            skPoint(sketch, "E710.MirrorP", {"position": v(41.08, -37.2) * mm});
            skPoint(sketch, "E711.MirrorP", {"position": v(7.6, -42) * mm});
            skPoint(sketch, "E712.MirrorP", {"position": v(6.06, -39.26) * mm});
            skLineSegment(sketch, "E713.MirrorCS", {"start": v(11.06, -46.26) * mm, "end": v(9.7, -44.89) * mm});
            skLineSegment(sketch, "E714.MirrorCS", {"start": v(27.43, -50.97) * mm, "end": v(27.43, -53.71) * mm});
            skPoint(sketch, "E715.MirrorP", {"position": v(25.62, -54.46) * mm});
            skLineSegment(sketch, "E716.MirrorCS", {"start": v(18.66, -54.14) * mm, "end": v(20.47, -54.46) * mm, "construction": true});
            skPoint(sketch, "E717.MirrorP", {"position": v(11.5, -46.69) * mm});
            skPoint(sketch, "E718.MirrorP", {"position": v(36.82, -44.46) * mm});
            skLineSegment(sketch, "E719.MirrorCS", {"start": v(24.93, -50.8) * mm, "end": v(26.84, -50.47) * mm});
            skPoint(sketch, "E720.MirrorP", {"position": v(38.48, -42) * mm});
            skPoint(sketch, "E721.MirrorP", {"position": v(45.1, -35.23) * mm});
            skPoint(sketch, "E722.MirrorP", {"position": v(5.68, -37.48) * mm});
            skLineSegment(sketch, "E723.MirrorCS", {"start": v(4.45, -43.11) * mm, "end": v(7.04, -42.2) * mm});
            skPoint(sketch, "E724.MirrorP", {"position": v(29.92, -49.57) * mm});
            skPoint(sketch, "E725.MirrorP", {"position": v(8.4, -48.85) * mm});
            skLineSegment(sketch, "E726.MirrorCS", {"start": v(5.6, -39.64) * mm, "end": v(3.48, -41.38) * mm});
            skLineSegment(sketch, "E727.MirrorCS", {"start": v(7.31, -41.48) * mm, "end": v(6.36, -39.79) * mm});
            skPoint(sketch, "E728.MirrorP", {"position": v(3.15, -41.65) * mm});
            skLineSegment(sketch, "E729.MirrorCS", {"start": v(2.34, -37.48) * mm, "end": v(5.08, -37.48) * mm});
            skSolve(sketch);
        }
        {
            var Q0;
            Q0 = qSketchRegion(id + "F0", true);
            extrude(context, id + "F2", {"entities" : qUnion([Q0]), "depth" : 6.35 * mm});
        }
        {
            var Q0;
            Q0 = qSketchRegion(id + "F1", true);
            extrude(context, id + "F3", {"entities" : qUnion([Q0]), "depth" : 6.35 * mm});
        }
    });
